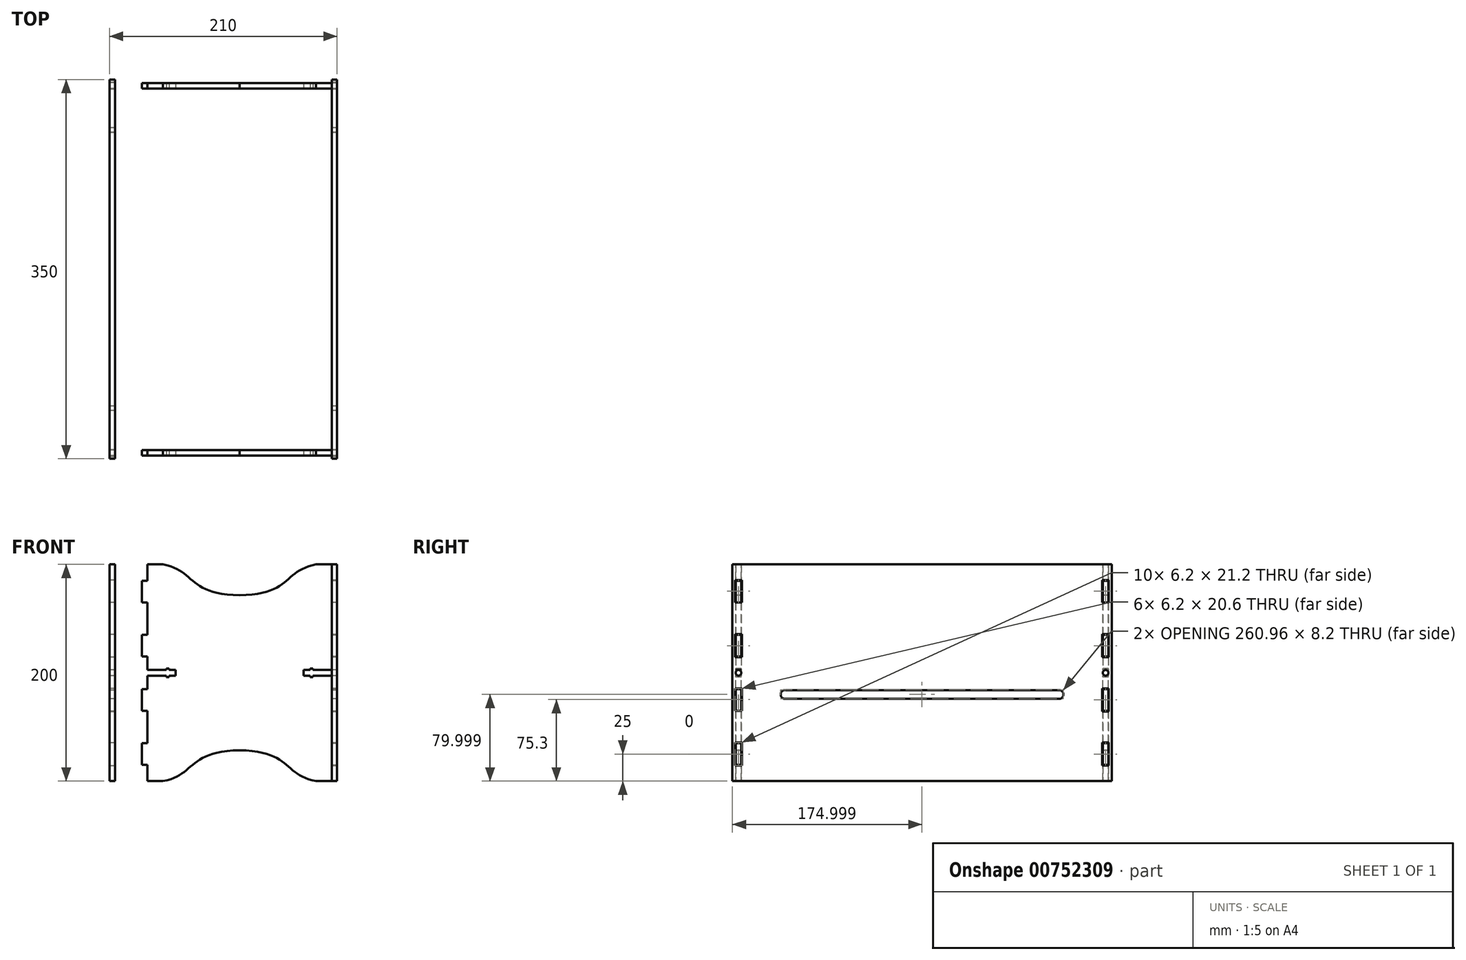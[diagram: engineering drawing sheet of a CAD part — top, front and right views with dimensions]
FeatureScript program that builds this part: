
annotation { "Feature Type Name" : "Feature", "Feature Type Description" : "" }
export const myFeature = defineFeature(function(context is Context, id is Id, definition is map)
    precondition{}
    {
        {
            var Q0;
            Q0=qCreatedBy(makeId("Right.planeOp"),FACE);
            var sketch = newSketch(context, id + "F0", { "sketchPlane" : qUnion([Q0])});
            skLineSegment(sketch, "E0.bottom", {"start": v(175, -100) * mm, "end": v(-175, -100) * mm});
            skLineSegment(sketch, "E0.top", {"start": v(175, 100) * mm, "end": v(4, 100) * mm});
            skLineSegment(sketch, "E0.left", {"start": v(175, -100) * mm, "end": v(175, 100) * mm});
            skLineSegment(sketch, "E0.right", {"start": v(-175, -100) * mm, "end": v(-175, 100) * mm});
            skPoint(sketch, "E0.middle", {"position": v(0, 0) * mm});
            skLineSegment(sketch, "E1", {"start": v(0, 80) * mm, "end": v(0, -100) * mm, "construction": true});
            skLineSegment(sketch, "E2", {"start": v(-175, 0) * mm, "end": v(175, 0) * mm, "construction": true});
            skLineSegment(sketch, "E3.trimOffspring", {"start": v(-4, 100) * mm, "end": v(-175, 100) * mm});
            skLineSegment(sketch, "E4", {"start": v(-172, 100) * mm, "end": v(-172, 85) * mm, "construction": true});
            skLineSegment(sketch, "E5", {"start": v(-166.8, 65) * mm, "end": v(-166.8, 35) * mm, "construction": true});
            skLineSegment(sketch, "E6.bottom", {"start": v(-172, 85) * mm, "end": v(-166.8, 85) * mm});
            skLineSegment(sketch, "E6.top", {"start": v(-172, 65) * mm, "end": v(-166.8, 65) * mm});
            skLineSegment(sketch, "E6.left", {"start": v(-172, 85) * mm, "end": v(-172, 65) * mm});
            skLineSegment(sketch, "E6.right", {"start": v(-166.8, 85) * mm, "end": v(-166.8, 65) * mm});
            skLineSegment(sketch, "E7.bottom", {"start": v(-172, 35) * mm, "end": v(-166.8, 35) * mm});
            skLineSegment(sketch, "E7.top", {"start": v(-172, 15) * mm, "end": v(-166.8, 15) * mm});
            skLineSegment(sketch, "E7.left", {"start": v(-172, 35) * mm, "end": v(-172, 15) * mm});
            skLineSegment(sketch, "E7.right", {"start": v(-166.8, 35) * mm, "end": v(-166.8, 15) * mm});
            skLineSegment(sketch, "E8", {"start": v(-169.4, 65) * mm, "end": v(-169.4, 35) * mm, "construction": true});
            skPoint(sketch, "E9", {"position": v(-169.4, 50) * mm});
            skLineSegment(sketch, "E10.MirrorCS", {"start": v(-172, -85) * mm, "end": v(-166.8, -85) * mm});
            skPoint(sketch, "E11.orphan", {"position": v(-166.8, 100) * mm});
            skLineSegment(sketch, "E12.trimOffspring", {"start": v(-172, 65) * mm, "end": v(-172, 35) * mm, "construction": true});
            skLineSegment(sketch, "E13.MirrorCS", {"start": v(-166.8, -85) * mm, "end": v(-166.8, -65) * mm});
            skLineSegment(sketch, "E14.MirrorCS", {"start": v(-172, -85) * mm, "end": v(-172, -65) * mm});
            skLineSegment(sketch, "E15.MirrorCS", {"start": v(-172, -65) * mm, "end": v(-166.8, -65) * mm});
            skLineSegment(sketch, "E16.MirrorCS", {"start": v(-172, -35) * mm, "end": v(-166.8, -35) * mm});
            skLineSegment(sketch, "E17.MirrorCS", {"start": v(-172, -15) * mm, "end": v(-166.8, -15) * mm});
            skLineSegment(sketch, "E18.trimOffspring", {"start": v(-172, 0) * mm, "end": v(-172, -15) * mm, "construction": true});
            skLineSegment(sketch, "E19.trimOffspring", {"start": v(-166.8, 0) * mm, "end": v(-166.8, -15) * mm, "construction": true});
            skLineSegment(sketch, "E20.MirrorCS", {"start": v(-172, -35) * mm, "end": v(-172, -15) * mm});
            skLineSegment(sketch, "E21.MirrorCS", {"start": v(-166.8, -35) * mm, "end": v(-166.8, -15) * mm});
            skLineSegment(sketch, "E22.trimOffspring", {"start": v(-172, -35) * mm, "end": v(-172, -65) * mm, "construction": true});
            skLineSegment(sketch, "E23.trimOffspring", {"start": v(-166.8, -35) * mm, "end": v(-166.8, -65) * mm, "construction": true});
            skLineSegment(sketch, "E24.trimOffspring", {"start": v(-166.8, -85) * mm, "end": v(-166.8, -100) * mm, "construction": true});
            skLineSegment(sketch, "E25.trimOffspring", {"start": v(-172, -85) * mm, "end": v(-172, -100) * mm, "construction": true});
            skLineSegment(sketch, "E26.MirrorCS", {"start": v(172, 85) * mm, "end": v(172, 65) * mm});
            skLineSegment(sketch, "E27.MirrorCS", {"start": v(166.8, 85) * mm, "end": v(166.8, 65) * mm});
            skLineSegment(sketch, "E28.MirrorCS", {"start": v(172, 85) * mm, "end": v(166.8, 85) * mm});
            skLineSegment(sketch, "E29.MirrorCS", {"start": v(172, 65) * mm, "end": v(166.8, 65) * mm});
            skLineSegment(sketch, "E30.MirrorCS", {"start": v(172, 35) * mm, "end": v(166.8, 35) * mm});
            skLineSegment(sketch, "E31.MirrorCS", {"start": v(166.8, 35) * mm, "end": v(166.8, 15) * mm});
            skLineSegment(sketch, "E32.MirrorCS", {"start": v(172, 35) * mm, "end": v(172, 15) * mm});
            skLineSegment(sketch, "E33.MirrorCS", {"start": v(172, 15) * mm, "end": v(166.8, 15) * mm});
            skLineSegment(sketch, "E34.MirrorCS", {"start": v(172, -15) * mm, "end": v(166.8, -15) * mm});
            skLineSegment(sketch, "E35.MirrorCS", {"start": v(166.8, -35) * mm, "end": v(166.8, -15) * mm});
            skLineSegment(sketch, "E36.MirrorCS", {"start": v(172, -35) * mm, "end": v(172, -15) * mm});
            skLineSegment(sketch, "E37.MirrorCS", {"start": v(172, -35) * mm, "end": v(166.8, -35) * mm});
            skLineSegment(sketch, "E38.MirrorCS", {"start": v(172, -65) * mm, "end": v(166.8, -65) * mm});
            skLineSegment(sketch, "E39.MirrorCS", {"start": v(172, -85) * mm, "end": v(166.8, -85) * mm});
            skLineSegment(sketch, "E40.MirrorCS", {"start": v(166.8, -85) * mm, "end": v(166.8, -65) * mm});
            skLineSegment(sketch, "E41.MirrorCS", {"start": v(172, -85) * mm, "end": v(172, -65) * mm});
            skCircle(sketch, "E42", {"center": v(-126.38, -20) * mm, "radius": 4.1 * mm});
            skLineSegment(sketch, "E43.left", {"start": v(-126.26, -15.9) * mm, "end": v(-126.26, -24.1) * mm});
            skPoint(sketch, "E44.left.end.orphan", {"position": v(4, 80) * mm});
            skPoint(sketch, "E44.right.end.orphan", {"position": v(-4, 80) * mm});
            skLineSegment(sketch, "E45", {"start": v(-4, 100) * mm, "end": v(4, 100) * mm});
            skCircle(sketch, "E46", {"center": v(0, 80) * mm, "radius": 150 * mm, "construction": true});
            skPoint(sketch, "E43.right.end.orphan", {"position": v(140.09, -4.1) * mm});
            skPoint(sketch, "E47.center.orphan", {"position": v(140.09, 0) * mm});
            skCircle(sketch, "E48", {"center": v(-126.38, -20) * mm, "radius": 11 * mm, "construction": true});
            skCircle(sketch, "E49", {"center": v(126.38, -20) * mm, "radius": 4.1 * mm});
            skLineSegment(sketch, "E50.left", {"start": v(126.5, -15.9) * mm, "end": v(126.5, -24.1) * mm});
            skCircle(sketch, "E51", {"center": v(126.38, -20) * mm, "radius": 11 * mm, "construction": true});
            skLineSegment(sketch, "E52.bottom", {"start": v(126.5, -15.9) * mm, "end": v(-126.26, -15.9) * mm});
            skLineSegment(sketch, "E52.top", {"start": v(126.5, -24.1) * mm, "end": v(-126.26, -24.1) * mm});
            skCircle(sketch, "E53", {"center": v(-169.4, 0) * mm, "radius": 2.6 * mm});
            skCircle(sketch, "E54.MirrorC", {"center": v(169.4, 0) * mm, "radius": 2.6 * mm});
            skSolve(sketch);
        }
        {
            var Q0;
            Q0=qSketchRegion(id+"F0",true);
            extrude(context, id + "F1", {"entities" : qUnion([Q0]), "depth" : 5 * mm});
        }
        {
            var Q0;
            Q0=makeQuery(id+"F1.opExtrude","SWEPT_FACE",FACE,{"disambiguationData":[OSD([sQuery(id+"F0.wireOp",EDGE,"E27.MirrorCS")])]});
            var sketch = newSketch(context, id + "F2", { "sketchPlane" : qUnion([Q0])});
            skPoint(sketch, "E55.0", {"position": v(-5, 100) * mm});
            skLineSegment(sketch, "E56.bottom", {"start": v(0, 100) * mm, "end": v(14.33, 100) * mm});
            skLineSegment(sketch, "E56.top", {"start": v(0, -100) * mm, "end": v(14.33, -100) * mm});
            skLineSegment(sketch, "E56.left", {"start": v(-5, 85) * mm, "end": v(-5, 65) * mm});
            skLineSegment(sketch, "E56.right", {"start": v(170, 100) * mm, "end": v(170, 52.6) * mm});
            skPoint(sketch, "E57.middle", {"position": v(18.7, -50) * mm});
            skPoint(sketch, "E57.centerSnap0", {"position": v(26, -50) * mm});
            skLineSegment(sketch, "E58.0", {"start": v(0, 85) * mm, "end": v(0, 65) * mm, "construction": true});
            skLineSegment(sketch, "E58.1", {"start": v(0, 35) * mm, "end": v(0, 15) * mm, "construction": true});
            skLineSegment(sketch, "E58.2", {"start": v(0, -35) * mm, "end": v(0, -15) * mm, "construction": true});
            skLineSegment(sketch, "E58.3", {"start": v(0, -85) * mm, "end": v(0, -65) * mm, "construction": true});
            skLineSegment(sketch, "E59.bottom", {"start": v(0, 85) * mm, "end": v(-5, 85) * mm});
            skLineSegment(sketch, "E59.left", {"start": v(0, 85) * mm, "end": v(0, 100) * mm});
            skLineSegment(sketch, "E60.bottom", {"start": v(0, 65) * mm, "end": v(-5, 65) * mm});
            skLineSegment(sketch, "E60.top", {"start": v(0, 35) * mm, "end": v(-5, 35) * mm});
            skLineSegment(sketch, "E60.left", {"start": v(0, 65) * mm, "end": v(0, 52.6) * mm});
            skLineSegment(sketch, "E61.bottom", {"start": v(0, 15) * mm, "end": v(0, 15) * mm});
            skLineSegment(sketch, "E61.top", {"start": v(0, -15) * mm, "end": v(0, -15) * mm});
            skLineSegment(sketch, "E61.right", {"start": v(0, 15) * mm, "end": v(0, 2.6) * mm});
            skLineSegment(sketch, "E62.bottom", {"start": v(-5, -15) * mm, "end": v(0, -15) * mm});
            skLineSegment(sketch, "E62.top", {"start": v(-5, 15) * mm, "end": v(0, 15) * mm});
            skLineSegment(sketch, "E62.right", {"start": v(0, -15) * mm, "end": v(0, -2.6) * mm});
            skLineSegment(sketch, "E63", {"start": v(0, -35) * mm, "end": v(-5, -35) * mm});
            skLineSegment(sketch, "E64", {"start": v(0, -85) * mm, "end": v(-5, -85) * mm});
            skLineSegment(sketch, "E65", {"start": v(0, -65) * mm, "end": v(-5, -65) * mm});
            skLineSegment(sketch, "E66.trimOffspring", {"start": v(-5, -15) * mm, "end": v(-5, -35) * mm});
            skLineSegment(sketch, "E67.trimOffspring", {"start": v(-5, -65) * mm, "end": v(-5, -85) * mm});
            skLineSegment(sketch, "E68", {"start": v(0, -85) * mm, "end": v(0, -100) * mm});
            skLineSegment(sketch, "E69", {"start": v(0, -52.6) * mm, "end": v(0, -65) * mm});
            skLineSegment(sketch, "E70", {"start": v(0, -47.4) * mm, "end": v(0, -35) * mm});
            skLineSegment(sketch, "E71", {"start": v(0, 35) * mm, "end": v(0, 47.4) * mm});
            skLineSegment(sketch, "E72", {"start": v(0, 52.6) * mm, "end": v(0, 65) * mm});
            skLineSegment(sketch, "E73.trimOffspring", {"start": v(0, 47.4) * mm, "end": v(0, 35) * mm});
            skLineSegment(sketch, "E74", {"start": v(-5, 65) * mm, "end": v(0, 65) * mm});
            skLineSegment(sketch, "E75.trimOffspring", {"start": v(-5, 35) * mm, "end": v(-5, 15) * mm});
            skLineSegment(sketch, "E76", {"start": v(85, 100) * mm, "end": v(85, -100) * mm, "construction": true});
            skLineSegment(sketch, "E77.MirrorCS", {"start": v(175, 65) * mm, "end": v(170, 65) * mm});
            skLineSegment(sketch, "E78.MirrorCS", {"start": v(170, 65) * mm, "end": v(175, 65) * mm});
            skLineSegment(sketch, "E79.MirrorCS", {"start": v(170, 85) * mm, "end": v(175, 85) * mm});
            skLineSegment(sketch, "E80.MirrorCS", {"start": v(175, -15) * mm, "end": v(170, -15) * mm});
            skLineSegment(sketch, "E81.MirrorCS", {"start": v(170, -15) * mm, "end": v(170, -2.6) * mm});
            skLineSegment(sketch, "E82.MirrorCS", {"start": v(175, 15) * mm, "end": v(170, 15) * mm});
            skLineSegment(sketch, "E83.MirrorCS", {"start": v(170, -35) * mm, "end": v(175, -35) * mm});
            skLineSegment(sketch, "E84.MirrorCS", {"start": v(170, 35) * mm, "end": v(175, 35) * mm});
            skLineSegment(sketch, "E85.MirrorCS", {"start": v(170, -65) * mm, "end": v(175, -65) * mm});
            skLineSegment(sketch, "E86.MirrorCS", {"start": v(170, -85) * mm, "end": v(175, -85) * mm});
            skLineSegment(sketch, "E87.MirrorCS", {"start": v(170, 52.6) * mm, "end": v(170, 65) * mm});
            skLineSegment(sketch, "E88.MirrorCS", {"start": v(170, 35) * mm, "end": v(170, 47.4) * mm});
            skLineSegment(sketch, "E89.MirrorCS", {"start": v(175, 85) * mm, "end": v(175, 65) * mm});
            skLineSegment(sketch, "E90.MirrorCS", {"start": v(170, 100) * mm, "end": v(170, 15) * mm});
            skLineSegment(sketch, "E91.MirrorCS", {"start": v(170, -15) * mm, "end": v(170, -15) * mm});
            skLineSegment(sketch, "E92.MirrorCS", {"start": v(170, 85) * mm, "end": v(170, 100) * mm});
            skPoint(sketch, "E93.MirrorP", {"position": v(175, 100) * mm});
            skLineSegment(sketch, "E94.MirrorCS", {"start": v(170, -47.4) * mm, "end": v(170, -35) * mm});
            skLineSegment(sketch, "E95.MirrorCS", {"start": v(175, -15) * mm, "end": v(175, -35) * mm});
            skLineSegment(sketch, "E96.MirrorCS", {"start": v(170, 47.4) * mm, "end": v(170, 35) * mm});
            skLineSegment(sketch, "E97.MirrorCS", {"start": v(170, -85) * mm, "end": v(170, -100) * mm});
            skLineSegment(sketch, "E98.MirrorCS", {"start": v(170, 15) * mm, "end": v(170, 15) * mm});
            skLineSegment(sketch, "E99.MirrorCS", {"start": v(170, -52.6) * mm, "end": v(170, -65) * mm});
            skLineSegment(sketch, "E100.MirrorCS", {"start": v(170, 65) * mm, "end": v(170, 52.6) * mm});
            skLineSegment(sketch, "E101.MirrorCS", {"start": v(175, 35) * mm, "end": v(175, 15) * mm});
            skLineSegment(sketch, "E102.MirrorCS", {"start": v(175, -65) * mm, "end": v(175, -85) * mm});
            skLineSegment(sketch, "E103.MirrorCS", {"start": v(170, 85) * mm, "end": v(170, 65) * mm, "construction": true});
            skFitSpline(sketch, "E104", {"points": [v(14.33, 100) * mm, v(85, 71.5) * mm], "startDerivative": vector(91.37, -16.34) * mm, "endDerivative": vector(146.95, -3.2) * mm});
            skFitSpline(sketch, "E105.MirrorCS", {"points": [v(155.67, 100) * mm, v(85, 71.5) * mm], "startDerivative": vector(-91.37, -16.34) * mm, "endDerivative": vector(-146.95, -3.2) * mm});
            skLineSegment(sketch, "E106.trimOffspring", {"start": v(155.67, 100) * mm, "end": v(170, 100) * mm});
            skLineSegment(sketch, "E107", {"start": v(85, 0) * mm, "end": v(170, 0) * mm, "construction": true});
            skFitSpline(sketch, "E108.MirrorCS", {"points": [v(155.67, -100) * mm, v(85, -71.5) * mm], "startDerivative": vector(-91.37, 16.34) * mm, "endDerivative": vector(-146.95, 3.2) * mm});
            skFitSpline(sketch, "E109.MirrorCS", {"points": [v(14.33, -100) * mm, v(85, -71.5) * mm], "startDerivative": vector(91.37, 16.34) * mm, "endDerivative": vector(146.95, 3.2) * mm});
            skLineSegment(sketch, "E110.trimOffspring", {"start": v(155.67, -100) * mm, "end": v(170, -100) * mm});
            skLineSegment(sketch, "E111.trimOffspring", {"start": v(170, 42.3) * mm, "end": v(170, 2.6) * mm});
            skLineSegment(sketch, "E112.bottom", {"start": v(0, 2.6) * mm, "end": v(17.4, 2.6) * mm});
            skLineSegment(sketch, "E112.top", {"start": v(0, -2.6) * mm, "end": v(17.4, -2.6) * mm});
            skLineSegment(sketch, "E112.right", {"start": v(26, 2.6) * mm, "end": v(26, -2.6) * mm});
            skLineSegment(sketch, "E113.bottom", {"start": v(20, -4.05) * mm, "end": v(17.4, -4.05) * mm});
            skLineSegment(sketch, "E113.top", {"start": v(20, 4.05) * mm, "end": v(17.4, 4.05) * mm});
            skLineSegment(sketch, "E113.left", {"start": v(20, -4.05) * mm, "end": v(20, -2.6) * mm});
            skLineSegment(sketch, "E113.right", {"start": v(17.4, -4.05) * mm, "end": v(17.4, -2.6) * mm});
            skPoint(sketch, "E113.middle", {"position": v(18.7, 0) * mm});
            skPoint(sketch, "E113.middle.positionSnap0", {"position": v(26, 0) * mm});
            skPoint(sketch, "E113.centerSnap0", {"position": v(26, 0) * mm});
            skLineSegment(sketch, "E114.trimOffspring", {"start": v(17.4, 2.6) * mm, "end": v(17.4, 4.05) * mm});
            skLineSegment(sketch, "E115.trimOffspring", {"start": v(20, 2.6) * mm, "end": v(26, 2.6) * mm});
            skLineSegment(sketch, "E116.trimOffspring", {"start": v(20, 2.6) * mm, "end": v(20, 4.05) * mm});
            skLineSegment(sketch, "E117.trimOffspring", {"start": v(20, -2.6) * mm, "end": v(26, -2.6) * mm});
            skPoint(sketch, "E118.MirrorP", {"position": v(174, 0) * mm});
            skLineSegment(sketch, "E119.MirrorCS", {"start": v(170, 92.3) * mm, "end": v(170, 79.9) * mm});
            skPoint(sketch, "E120.MirrorP", {"position": v(181.3, 0) * mm});
            skLineSegment(sketch, "E121", {"start": v(0, 52.6) * mm, "end": v(0, 47.4) * mm});
            skLineSegment(sketch, "E122", {"start": v(0, -47.4) * mm, "end": v(0, -52.6) * mm});
            skLineSegment(sketch, "E123", {"start": v(170, -52.6) * mm, "end": v(170, -47.4) * mm});
            skLineSegment(sketch, "E124", {"start": v(170, 47.4) * mm, "end": v(170, 52.6) * mm});
            skLineSegment(sketch, "E125.trimOffspring", {"start": v(0, -2.6) * mm, "end": v(0, -15) * mm});
            skLineSegment(sketch, "E126.trimOffspring", {"start": v(170, 92.3) * mm, "end": v(170, 2.6) * mm});
            skLineSegment(sketch, "E127.trimOffspring", {"start": v(170, 15) * mm, "end": v(170, 100) * mm});
            skLineSegment(sketch, "E128.trimOffspring", {"start": v(0, 2.6) * mm, "end": v(0, 15) * mm});
            skLineSegment(sketch, "E129.bottom", {"start": v(170, -2.6) * mm, "end": v(152.6, -2.6) * mm});
            skLineSegment(sketch, "E129.top", {"start": v(170, 2.6) * mm, "end": v(152.6, 2.6) * mm});
            skLineSegment(sketch, "E129.right", {"start": v(144, -2.6) * mm, "end": v(144, 2.6) * mm});
            skLineSegment(sketch, "E130.bottom", {"start": v(150, 4.05) * mm, "end": v(152.6, 4.05) * mm});
            skLineSegment(sketch, "E130.top", {"start": v(150, -4.05) * mm, "end": v(152.6, -4.05) * mm});
            skLineSegment(sketch, "E130.left", {"start": v(150, 4.05) * mm, "end": v(150, 2.6) * mm});
            skLineSegment(sketch, "E130.right", {"start": v(152.6, 4.05) * mm, "end": v(152.6, 2.6) * mm});
            skLineSegment(sketch, "E131.trimOffspring", {"start": v(152.6, -2.6) * mm, "end": v(152.6, -4.05) * mm});
            skLineSegment(sketch, "E132.trimOffspring", {"start": v(150, -2.6) * mm, "end": v(144, -2.6) * mm});
            skLineSegment(sketch, "E133.trimOffspring", {"start": v(150, -2.6) * mm, "end": v(150, -4.05) * mm});
            skLineSegment(sketch, "E134.trimOffspring", {"start": v(150, 2.6) * mm, "end": v(144, 2.6) * mm});
            skLineSegment(sketch, "E135.trimOffspring", {"start": v(170, -2.6) * mm, "end": v(170, -47.4) * mm});
            skLineSegment(sketch, "E136.trimOffspring", {"start": v(170, -2.6) * mm, "end": v(170, -15) * mm});
            skLineSegment(sketch, "E137.trimOffspring", {"start": v(170, 2.6) * mm, "end": v(170, 92.3) * mm});
            skLineSegment(sketch, "E138.trimOffspring", {"start": v(170, -2.6) * mm, "end": v(170, -100) * mm});
            skSolve(sketch);
        }
        {
            var Q0;
            Q0=qSketchRegion(id+"F2",true);
            extrude(context, id + "F3", {"entities" : qUnion([Q0]), "depth" : 5 * mm});
        }
        {
            var Q0;
            Q0=makeQuery(id+"F3.opExtrude","SWEPT_BODY",BODY,{"disambiguationData":[OSD([sQuery(id+"F2.wireOp",EDGE,"E56.bottom"),sQuery(id+"F2.wireOp",EDGE,"E56.top"),sQuery(id+"F2.wireOp",EDGE,"SfhTXy7u-tcII-MEaY-9RSd-v6Q0Sdl2hSPR.bottom"),sQuery(id+"F2.wireOp",EDGE,"SfhTXy7u-tcII-MEaY-9RSd-v6Q0Sdl2hSPR.top"),sQuery(id+"F2.wireOp",EDGE,"SfhTXy7u-tcII-MEaY-9RSd-v6Q0Sdl2hSPR.right"),sQuery(id+"F2.wireOp",EDGE,"RLKNdBM9-fcir-abDg-scLo-AlFl0wZaGOfU.bottom"),sQuery(id+"F2.wireOp",EDGE,"RLKNdBM9-fcir-abDg-scLo-AlFl0wZaGOfU.top"),sQuery(id+"F2.wireOp",EDGE,"RLKNdBM9-fcir-abDg-scLo-AlFl0wZaGOfU.left"),sQuery(id+"F2.wireOp",EDGE,"RLKNdBM9-fcir-abDg-scLo-AlFl0wZaGOfU.right"),sQuery(id+"F2.wireOp",EDGE,"592e8475-5e9e-4e55-86be-326854908ba4.bottom"),sQuery(id+"F2.wireOp",EDGE,"592e8475-5e9e-4e55-86be-326854908ba4.top"),sQuery(id+"F2.wireOp",EDGE,"592e8475-5e9e-4e55-86be-326854908ba4.right"),sQuery(id+"F2.wireOp",EDGE,"E57.bottom"),sQuery(id+"F2.wireOp",EDGE,"E57.top"),sQuery(id+"F2.wireOp",EDGE,"E57.left"),sQuery(id+"F2.wireOp",EDGE,"E57.right"),sQuery(id+"F2.wireOp",EDGE,"98f910ef-10bf-4355-9089-b64edb675ca1.trimOffspring"),sQuery(id+"F2.wireOp",EDGE,"7f1d8590-854d-48a8-a345-113ac86432ce.trimOffspring"),sQuery(id+"F2.wireOp",EDGE,"8eb6f7d6-6f97-4ebc-a51c-8934afb20485.trimOffspring"),sQuery(id+"F2.wireOp",EDGE,"79887d4c-0bb1-4e3d-a504-848fb675985f.trimOffspring"),sQuery(id+"F2.wireOp",EDGE,"6021e146-63f0-49d4-b214-f61fa3b2a401.trimOffspring"),sQuery(id+"F2.wireOp",EDGE,"bdb7ae41-a7ed-46e7-8485-b54428fed669.trimOffspring"),sQuery(id+"F2.wireOp",EDGE,"45a4283d-6044-4d88-b901-0b074d01a6ab.trimOffspring"),sQuery(id+"F2.wireOp",EDGE,"59fc1645-d4a0-4682-934b-e6e005b09d3d.trimOffspring"),sQuery(id+"F2.wireOp",EDGE,"E59.bottom"),sQuery(id+"F2.wireOp",EDGE,"E59.left"),sQuery(id+"F2.wireOp",EDGE,"E60.top"),sQuery(id+"F2.wireOp",EDGE,"E62.bottom"),sQuery(id+"F2.wireOp",EDGE,"E62.top"),sQuery(id+"F2.wireOp",EDGE,"E62.right"),sQuery(id+"F2.wireOp",EDGE,"E63"),sQuery(id+"F2.wireOp",EDGE,"E64"),sQuery(id+"F2.wireOp",EDGE,"E65"),sQuery(id+"F2.wireOp",EDGE,"E66.trimOffspring"),sQuery(id+"F2.wireOp",EDGE,"E67.trimOffspring"),sQuery(id+"F2.wireOp",EDGE,"E68"),sQuery(id+"F2.wireOp",EDGE,"E69"),sQuery(id+"F2.wireOp",EDGE,"E70"),sQuery(id+"F2.wireOp",EDGE,"E72"),sQuery(id+"F2.wireOp",EDGE,"E73.trimOffspring"),sQuery(id+"F2.wireOp",EDGE,"E56.left"),sQuery(id+"F2.wireOp",EDGE,"E74"),sQuery(id+"F2.wireOp",EDGE,"E75.trimOffspring"),sQuery(id+"F2.wireOp",EDGE,"729de1fe-793c-4f06-af17-d50d40598c080.MirrorCS"),sQuery(id+"F2.wireOp",EDGE,"729de1fe-793c-4f06-af17-d50d40598c082.MirrorCS"),sQuery(id+"F2.wireOp",EDGE,"729de1fe-793c-4f06-af17-d50d40598c083.MirrorCS"),sQuery(id+"F2.wireOp",EDGE,"729de1fe-793c-4f06-af17-d50d40598c084.MirrorCS"),sQuery(id+"F2.wireOp",EDGE,"729de1fe-793c-4f06-af17-d50d40598c085.MirrorCS"),sQuery(id+"F2.wireOp",EDGE,"729de1fe-793c-4f06-af17-d50d40598c086.MirrorCS"),sQuery(id+"F2.wireOp",EDGE,"729de1fe-793c-4f06-af17-d50d40598c087.MirrorCS"),sQuery(id+"F2.wireOp",EDGE,"729de1fe-793c-4f06-af17-d50d40598c088.MirrorCS"),sQuery(id+"F2.wireOp",EDGE,"729de1fe-793c-4f06-af17-d50d40598c089.MirrorCS"),sQuery(id+"F2.wireOp",EDGE,"E770.MirrorCS"),sQuery(id+"F2.wireOp",EDGE,"E78.MirrorCS"),sQuery(id+"F2.wireOp",EDGE,"E772.MirrorCS"),sQuery(id+"F2.wireOp",EDGE,"E79.MirrorCS"),sQuery(id+"F2.wireOp",EDGE,"E774.MirrorCS"),sQuery(id+"F2.wireOp",EDGE,"E775.MirrorCS"),sQuery(id+"F2.wireOp",EDGE,"E776.MirrorCS"),sQuery(id+"F2.wireOp",EDGE,"E777.MirrorCS"),sQuery(id+"F2.wireOp",EDGE,"E778.MirrorCS"),sQuery(id+"F2.wireOp",EDGE,"E779.MirrorCS"),sQuery(id+"F2.wireOp",EDGE,"729de1fe-793c-4f06-af17-d50d40598c0820.MirrorCS"),sQuery(id+"F2.wireOp",EDGE,"E80.MirrorCS"),sQuery(id+"F2.wireOp",EDGE,"E82.MirrorCS"),sQuery(id+"F2.wireOp",EDGE,"E83.MirrorCS"),sQuery(id+"F2.wireOp",EDGE,"E84.MirrorCS"),sQuery(id+"F2.wireOp",EDGE,"E85.MirrorCS"),sQuery(id+"F2.wireOp",EDGE,"E86.MirrorCS"),sQuery(id+"F2.wireOp",EDGE,"E92.MirrorCS"),sQuery(id+"F2.wireOp",EDGE,"729de1fe-793c-4f06-af17-d50d40598c0837.MirrorCS"),sQuery(id+"F2.wireOp",EDGE,"729de1fe-793c-4f06-af17-d50d40598c0838.MirrorCS"),sQuery(id+"F2.wireOp",EDGE,"729de1fe-793c-4f06-af17-d50d40598c0841.MirrorCS"),sQuery(id+"F2.wireOp",EDGE,"E95.MirrorCS"),sQuery(id+"F2.wireOp",EDGE,"729de1fe-793c-4f06-af17-d50d40598c0851.MirrorCS"),sQuery(id+"F2.wireOp",EDGE,"E89.MirrorCS"),sQuery(id+"F2.wireOp",EDGE,"E100.MirrorCS"),sQuery(id+"F2.wireOp",EDGE,"E101.MirrorCS"),sQuery(id+"F2.wireOp",EDGE,"E102.MirrorCS"),sQuery(id+"F2.wireOp",EDGE,"E104"),sQuery(id+"F2.wireOp",EDGE,"E105.MirrorCS"),sQuery(id+"F2.wireOp",EDGE,"E106.trimOffspring"),sQuery(id+"F2.wireOp",EDGE,"E108.MirrorCS"),sQuery(id+"F2.wireOp",EDGE,"E109.MirrorCS"),sQuery(id+"F2.wireOp",EDGE,"E110.trimOffspring"),sQuery(id+"F2.wireOp",EDGE,"31b2c9c2-f7eb-4751-8350-943a16306e17.trimOffspring"),sQuery(id+"F2.wireOp",EDGE,"E111.trimOffspring")])]});
            var Q1;
            Q1=makeQuery(id+"F1.opExtrude","SWEPT_BODY",BODY,{"disambiguationData":[OSD([sQuery(id+"F0.wireOp",EDGE,"E0.bottom"),sQuery(id+"F0.wireOp",EDGE,"E0.top"),sQuery(id+"F0.wireOp",EDGE,"E0.left"),sQuery(id+"F0.wireOp",EDGE,"E0.right"),sQuery(id+"F0.wireOp",EDGE,"E3.trimOffspring"),sQuery(id+"F0.wireOp",EDGE,"E6.bottom"),sQuery(id+"F0.wireOp",EDGE,"E6.top"),sQuery(id+"F0.wireOp",EDGE,"E6.left"),sQuery(id+"F0.wireOp",EDGE,"E6.right"),sQuery(id+"F0.wireOp",EDGE,"E7.bottom"),sQuery(id+"F0.wireOp",EDGE,"E7.top"),sQuery(id+"F0.wireOp",EDGE,"E7.left"),sQuery(id+"F0.wireOp",EDGE,"E7.right"),sQuery(id+"F0.wireOp",EDGE,"1BBTkZs5-luX3-xtZO-tfno-nD7ZldyCOrRv"),sQuery(id+"F0.wireOp",EDGE,"E13.MirrorCS"),sQuery(id+"F0.wireOp",EDGE,"E14.MirrorCS"),sQuery(id+"F0.wireOp",EDGE,"E10.MirrorCS"),sQuery(id+"F0.wireOp",EDGE,"E15.MirrorCS"),sQuery(id+"F0.wireOp",EDGE,"edba22f7-fcec-4b76-9e19-08ec19d2e6a00.MirrorC"),sQuery(id+"F0.wireOp",EDGE,"E16.MirrorCS"),sQuery(id+"F0.wireOp",EDGE,"E17.MirrorCS"),sQuery(id+"F0.wireOp",EDGE,"E20.MirrorCS"),sQuery(id+"F0.wireOp",EDGE,"E21.MirrorCS"),sQuery(id+"F0.wireOp",EDGE,"E26.MirrorCS"),sQuery(id+"F0.wireOp",EDGE,"E27.MirrorCS"),sQuery(id+"F0.wireOp",EDGE,"E28.MirrorCS"),sQuery(id+"F0.wireOp",EDGE,"E29.MirrorCS"),sQuery(id+"F0.wireOp",EDGE,"e9cac41d-f357-42ad-afaa-485d0ff043840.MirrorC"),sQuery(id+"F0.wireOp",EDGE,"E30.MirrorCS"),sQuery(id+"F0.wireOp",EDGE,"E31.MirrorCS"),sQuery(id+"F0.wireOp",EDGE,"E32.MirrorCS"),sQuery(id+"F0.wireOp",EDGE,"E33.MirrorCS"),sQuery(id+"F0.wireOp",EDGE,"E34.MirrorCS"),sQuery(id+"F0.wireOp",EDGE,"E35.MirrorCS"),sQuery(id+"F0.wireOp",EDGE,"E36.MirrorCS"),sQuery(id+"F0.wireOp",EDGE,"E37.MirrorCS"),sQuery(id+"F0.wireOp",EDGE,"f40b6c40-3a45-4a40-b477-66a71d50dfa00.MirrorC"),sQuery(id+"F0.wireOp",EDGE,"E38.MirrorCS"),sQuery(id+"F0.wireOp",EDGE,"E39.MirrorCS"),sQuery(id+"F0.wireOp",EDGE,"E40.MirrorCS"),sQuery(id+"F0.wireOp",EDGE,"E41.MirrorCS"),sQuery(id+"F0.wireOp",EDGE,"E44.left"),sQuery(id+"F0.wireOp",EDGE,"E44.right"),sQuery(id+"F0.wireOp",EDGE,"eyhBYY9M-95YG-LpN2-QZ7T-SWmW0xq0itgo")])]});
            var Q2;
            Q2=makeQuery(id+"F3.opExtrude","CAP_FACE",FACE,{"disambiguationData":[OSD([sQuery(id+"F2.wireOp",EDGE,"E56.bottom"),sQuery(id+"F2.wireOp",EDGE,"E56.top"),sQuery(id+"F2.wireOp",EDGE,"SfhTXy7u-tcII-MEaY-9RSd-v6Q0Sdl2hSPR.bottom"),sQuery(id+"F2.wireOp",EDGE,"SfhTXy7u-tcII-MEaY-9RSd-v6Q0Sdl2hSPR.top"),sQuery(id+"F2.wireOp",EDGE,"SfhTXy7u-tcII-MEaY-9RSd-v6Q0Sdl2hSPR.right"),sQuery(id+"F2.wireOp",EDGE,"RLKNdBM9-fcir-abDg-scLo-AlFl0wZaGOfU.bottom"),sQuery(id+"F2.wireOp",EDGE,"RLKNdBM9-fcir-abDg-scLo-AlFl0wZaGOfU.top"),sQuery(id+"F2.wireOp",EDGE,"RLKNdBM9-fcir-abDg-scLo-AlFl0wZaGOfU.left"),sQuery(id+"F2.wireOp",EDGE,"RLKNdBM9-fcir-abDg-scLo-AlFl0wZaGOfU.right"),sQuery(id+"F2.wireOp",EDGE,"592e8475-5e9e-4e55-86be-326854908ba4.bottom"),sQuery(id+"F2.wireOp",EDGE,"592e8475-5e9e-4e55-86be-326854908ba4.top"),sQuery(id+"F2.wireOp",EDGE,"592e8475-5e9e-4e55-86be-326854908ba4.right"),sQuery(id+"F2.wireOp",EDGE,"E57.bottom"),sQuery(id+"F2.wireOp",EDGE,"E57.top"),sQuery(id+"F2.wireOp",EDGE,"E57.left"),sQuery(id+"F2.wireOp",EDGE,"E57.right"),sQuery(id+"F2.wireOp",EDGE,"98f910ef-10bf-4355-9089-b64edb675ca1.trimOffspring"),sQuery(id+"F2.wireOp",EDGE,"7f1d8590-854d-48a8-a345-113ac86432ce.trimOffspring"),sQuery(id+"F2.wireOp",EDGE,"8eb6f7d6-6f97-4ebc-a51c-8934afb20485.trimOffspring"),sQuery(id+"F2.wireOp",EDGE,"79887d4c-0bb1-4e3d-a504-848fb675985f.trimOffspring"),sQuery(id+"F2.wireOp",EDGE,"6021e146-63f0-49d4-b214-f61fa3b2a401.trimOffspring"),sQuery(id+"F2.wireOp",EDGE,"bdb7ae41-a7ed-46e7-8485-b54428fed669.trimOffspring"),sQuery(id+"F2.wireOp",EDGE,"45a4283d-6044-4d88-b901-0b074d01a6ab.trimOffspring"),sQuery(id+"F2.wireOp",EDGE,"59fc1645-d4a0-4682-934b-e6e005b09d3d.trimOffspring"),sQuery(id+"F2.wireOp",EDGE,"E59.bottom"),sQuery(id+"F2.wireOp",EDGE,"E59.left"),sQuery(id+"F2.wireOp",EDGE,"E60.top"),sQuery(id+"F2.wireOp",EDGE,"E62.bottom"),sQuery(id+"F2.wireOp",EDGE,"E62.top"),sQuery(id+"F2.wireOp",EDGE,"E62.right"),sQuery(id+"F2.wireOp",EDGE,"E63"),sQuery(id+"F2.wireOp",EDGE,"E64"),sQuery(id+"F2.wireOp",EDGE,"E65"),sQuery(id+"F2.wireOp",EDGE,"E66.trimOffspring"),sQuery(id+"F2.wireOp",EDGE,"E67.trimOffspring"),sQuery(id+"F2.wireOp",EDGE,"E68"),sQuery(id+"F2.wireOp",EDGE,"E69"),sQuery(id+"F2.wireOp",EDGE,"E70"),sQuery(id+"F2.wireOp",EDGE,"E72"),sQuery(id+"F2.wireOp",EDGE,"E73.trimOffspring"),sQuery(id+"F2.wireOp",EDGE,"E56.left"),sQuery(id+"F2.wireOp",EDGE,"E74"),sQuery(id+"F2.wireOp",EDGE,"E75.trimOffspring"),sQuery(id+"F2.wireOp",EDGE,"729de1fe-793c-4f06-af17-d50d40598c080.MirrorCS"),sQuery(id+"F2.wireOp",EDGE,"729de1fe-793c-4f06-af17-d50d40598c082.MirrorCS"),sQuery(id+"F2.wireOp",EDGE,"729de1fe-793c-4f06-af17-d50d40598c083.MirrorCS"),sQuery(id+"F2.wireOp",EDGE,"729de1fe-793c-4f06-af17-d50d40598c084.MirrorCS"),sQuery(id+"F2.wireOp",EDGE,"729de1fe-793c-4f06-af17-d50d40598c085.MirrorCS"),sQuery(id+"F2.wireOp",EDGE,"729de1fe-793c-4f06-af17-d50d40598c086.MirrorCS"),sQuery(id+"F2.wireOp",EDGE,"729de1fe-793c-4f06-af17-d50d40598c087.MirrorCS"),sQuery(id+"F2.wireOp",EDGE,"729de1fe-793c-4f06-af17-d50d40598c088.MirrorCS"),sQuery(id+"F2.wireOp",EDGE,"729de1fe-793c-4f06-af17-d50d40598c089.MirrorCS"),sQuery(id+"F2.wireOp",EDGE,"E770.MirrorCS"),sQuery(id+"F2.wireOp",EDGE,"E78.MirrorCS"),sQuery(id+"F2.wireOp",EDGE,"E772.MirrorCS"),sQuery(id+"F2.wireOp",EDGE,"E79.MirrorCS"),sQuery(id+"F2.wireOp",EDGE,"E774.MirrorCS"),sQuery(id+"F2.wireOp",EDGE,"E775.MirrorCS"),sQuery(id+"F2.wireOp",EDGE,"E776.MirrorCS"),sQuery(id+"F2.wireOp",EDGE,"E777.MirrorCS"),sQuery(id+"F2.wireOp",EDGE,"E778.MirrorCS"),sQuery(id+"F2.wireOp",EDGE,"E779.MirrorCS"),sQuery(id+"F2.wireOp",EDGE,"729de1fe-793c-4f06-af17-d50d40598c0820.MirrorCS"),sQuery(id+"F2.wireOp",EDGE,"E80.MirrorCS"),sQuery(id+"F2.wireOp",EDGE,"E82.MirrorCS"),sQuery(id+"F2.wireOp",EDGE,"E83.MirrorCS"),sQuery(id+"F2.wireOp",EDGE,"E84.MirrorCS"),sQuery(id+"F2.wireOp",EDGE,"E85.MirrorCS"),sQuery(id+"F2.wireOp",EDGE,"E86.MirrorCS"),sQuery(id+"F2.wireOp",EDGE,"E92.MirrorCS"),sQuery(id+"F2.wireOp",EDGE,"729de1fe-793c-4f06-af17-d50d40598c0837.MirrorCS"),sQuery(id+"F2.wireOp",EDGE,"729de1fe-793c-4f06-af17-d50d40598c0838.MirrorCS"),sQuery(id+"F2.wireOp",EDGE,"729de1fe-793c-4f06-af17-d50d40598c0841.MirrorCS"),sQuery(id+"F2.wireOp",EDGE,"E95.MirrorCS"),sQuery(id+"F2.wireOp",EDGE,"729de1fe-793c-4f06-af17-d50d40598c0851.MirrorCS"),sQuery(id+"F2.wireOp",EDGE,"E89.MirrorCS"),sQuery(id+"F2.wireOp",EDGE,"E100.MirrorCS"),sQuery(id+"F2.wireOp",EDGE,"E101.MirrorCS"),sQuery(id+"F2.wireOp",EDGE,"E102.MirrorCS"),sQuery(id+"F2.wireOp",EDGE,"E104"),sQuery(id+"F2.wireOp",EDGE,"E105.MirrorCS"),sQuery(id+"F2.wireOp",EDGE,"E106.trimOffspring"),sQuery(id+"F2.wireOp",EDGE,"E108.MirrorCS"),sQuery(id+"F2.wireOp",EDGE,"E109.MirrorCS"),sQuery(id+"F2.wireOp",EDGE,"E110.trimOffspring"),sQuery(id+"F2.wireOp",EDGE,"31b2c9c2-f7eb-4751-8350-943a16306e17.trimOffspring"),sQuery(id+"F2.wireOp",EDGE,"E111.trimOffspring")])],"isStart":false});
            var Q3;
            Q3=makeQuery(id+"F3.opExtrude","CAP_FACE",FACE,{"disambiguationData":[OSD([sQuery(id+"F2.wireOp",EDGE,"E56.bottom"),sQuery(id+"F2.wireOp",EDGE,"E56.top"),sQuery(id+"F2.wireOp",EDGE,"SfhTXy7u-tcII-MEaY-9RSd-v6Q0Sdl2hSPR.bottom"),sQuery(id+"F2.wireOp",EDGE,"SfhTXy7u-tcII-MEaY-9RSd-v6Q0Sdl2hSPR.top"),sQuery(id+"F2.wireOp",EDGE,"SfhTXy7u-tcII-MEaY-9RSd-v6Q0Sdl2hSPR.right"),sQuery(id+"F2.wireOp",EDGE,"RLKNdBM9-fcir-abDg-scLo-AlFl0wZaGOfU.bottom"),sQuery(id+"F2.wireOp",EDGE,"RLKNdBM9-fcir-abDg-scLo-AlFl0wZaGOfU.top"),sQuery(id+"F2.wireOp",EDGE,"RLKNdBM9-fcir-abDg-scLo-AlFl0wZaGOfU.left"),sQuery(id+"F2.wireOp",EDGE,"RLKNdBM9-fcir-abDg-scLo-AlFl0wZaGOfU.right"),sQuery(id+"F2.wireOp",EDGE,"592e8475-5e9e-4e55-86be-326854908ba4.bottom"),sQuery(id+"F2.wireOp",EDGE,"592e8475-5e9e-4e55-86be-326854908ba4.top"),sQuery(id+"F2.wireOp",EDGE,"592e8475-5e9e-4e55-86be-326854908ba4.right"),sQuery(id+"F2.wireOp",EDGE,"E57.bottom"),sQuery(id+"F2.wireOp",EDGE,"E57.top"),sQuery(id+"F2.wireOp",EDGE,"E57.left"),sQuery(id+"F2.wireOp",EDGE,"E57.right"),sQuery(id+"F2.wireOp",EDGE,"98f910ef-10bf-4355-9089-b64edb675ca1.trimOffspring"),sQuery(id+"F2.wireOp",EDGE,"7f1d8590-854d-48a8-a345-113ac86432ce.trimOffspring"),sQuery(id+"F2.wireOp",EDGE,"8eb6f7d6-6f97-4ebc-a51c-8934afb20485.trimOffspring"),sQuery(id+"F2.wireOp",EDGE,"79887d4c-0bb1-4e3d-a504-848fb675985f.trimOffspring"),sQuery(id+"F2.wireOp",EDGE,"6021e146-63f0-49d4-b214-f61fa3b2a401.trimOffspring"),sQuery(id+"F2.wireOp",EDGE,"bdb7ae41-a7ed-46e7-8485-b54428fed669.trimOffspring"),sQuery(id+"F2.wireOp",EDGE,"45a4283d-6044-4d88-b901-0b074d01a6ab.trimOffspring"),sQuery(id+"F2.wireOp",EDGE,"59fc1645-d4a0-4682-934b-e6e005b09d3d.trimOffspring"),sQuery(id+"F2.wireOp",EDGE,"E59.bottom"),sQuery(id+"F2.wireOp",EDGE,"E59.left"),sQuery(id+"F2.wireOp",EDGE,"E60.top"),sQuery(id+"F2.wireOp",EDGE,"E62.bottom"),sQuery(id+"F2.wireOp",EDGE,"E62.top"),sQuery(id+"F2.wireOp",EDGE,"E62.right"),sQuery(id+"F2.wireOp",EDGE,"E63"),sQuery(id+"F2.wireOp",EDGE,"E64"),sQuery(id+"F2.wireOp",EDGE,"E65"),sQuery(id+"F2.wireOp",EDGE,"E66.trimOffspring"),sQuery(id+"F2.wireOp",EDGE,"E67.trimOffspring"),sQuery(id+"F2.wireOp",EDGE,"E68"),sQuery(id+"F2.wireOp",EDGE,"E69"),sQuery(id+"F2.wireOp",EDGE,"E70"),sQuery(id+"F2.wireOp",EDGE,"E72"),sQuery(id+"F2.wireOp",EDGE,"E73.trimOffspring"),sQuery(id+"F2.wireOp",EDGE,"E56.left"),sQuery(id+"F2.wireOp",EDGE,"E74"),sQuery(id+"F2.wireOp",EDGE,"E75.trimOffspring"),sQuery(id+"F2.wireOp",EDGE,"729de1fe-793c-4f06-af17-d50d40598c080.MirrorCS"),sQuery(id+"F2.wireOp",EDGE,"729de1fe-793c-4f06-af17-d50d40598c082.MirrorCS"),sQuery(id+"F2.wireOp",EDGE,"729de1fe-793c-4f06-af17-d50d40598c083.MirrorCS"),sQuery(id+"F2.wireOp",EDGE,"729de1fe-793c-4f06-af17-d50d40598c084.MirrorCS"),sQuery(id+"F2.wireOp",EDGE,"729de1fe-793c-4f06-af17-d50d40598c085.MirrorCS"),sQuery(id+"F2.wireOp",EDGE,"729de1fe-793c-4f06-af17-d50d40598c086.MirrorCS"),sQuery(id+"F2.wireOp",EDGE,"729de1fe-793c-4f06-af17-d50d40598c087.MirrorCS"),sQuery(id+"F2.wireOp",EDGE,"729de1fe-793c-4f06-af17-d50d40598c088.MirrorCS"),sQuery(id+"F2.wireOp",EDGE,"729de1fe-793c-4f06-af17-d50d40598c089.MirrorCS"),sQuery(id+"F2.wireOp",EDGE,"E770.MirrorCS"),sQuery(id+"F2.wireOp",EDGE,"E78.MirrorCS"),sQuery(id+"F2.wireOp",EDGE,"E772.MirrorCS"),sQuery(id+"F2.wireOp",EDGE,"E79.MirrorCS"),sQuery(id+"F2.wireOp",EDGE,"E774.MirrorCS"),sQuery(id+"F2.wireOp",EDGE,"E775.MirrorCS"),sQuery(id+"F2.wireOp",EDGE,"E776.MirrorCS"),sQuery(id+"F2.wireOp",EDGE,"E777.MirrorCS"),sQuery(id+"F2.wireOp",EDGE,"E778.MirrorCS"),sQuery(id+"F2.wireOp",EDGE,"E779.MirrorCS"),sQuery(id+"F2.wireOp",EDGE,"729de1fe-793c-4f06-af17-d50d40598c0820.MirrorCS"),sQuery(id+"F2.wireOp",EDGE,"E80.MirrorCS"),sQuery(id+"F2.wireOp",EDGE,"E82.MirrorCS"),sQuery(id+"F2.wireOp",EDGE,"E83.MirrorCS"),sQuery(id+"F2.wireOp",EDGE,"E84.MirrorCS"),sQuery(id+"F2.wireOp",EDGE,"E85.MirrorCS"),sQuery(id+"F2.wireOp",EDGE,"E86.MirrorCS"),sQuery(id+"F2.wireOp",EDGE,"E92.MirrorCS"),sQuery(id+"F2.wireOp",EDGE,"729de1fe-793c-4f06-af17-d50d40598c0837.MirrorCS"),sQuery(id+"F2.wireOp",EDGE,"729de1fe-793c-4f06-af17-d50d40598c0838.MirrorCS"),sQuery(id+"F2.wireOp",EDGE,"729de1fe-793c-4f06-af17-d50d40598c0841.MirrorCS"),sQuery(id+"F2.wireOp",EDGE,"E95.MirrorCS"),sQuery(id+"F2.wireOp",EDGE,"729de1fe-793c-4f06-af17-d50d40598c0851.MirrorCS"),sQuery(id+"F2.wireOp",EDGE,"E89.MirrorCS"),sQuery(id+"F2.wireOp",EDGE,"E100.MirrorCS"),sQuery(id+"F2.wireOp",EDGE,"E101.MirrorCS"),sQuery(id+"F2.wireOp",EDGE,"E102.MirrorCS"),sQuery(id+"F2.wireOp",EDGE,"E104"),sQuery(id+"F2.wireOp",EDGE,"E105.MirrorCS"),sQuery(id+"F2.wireOp",EDGE,"E106.trimOffspring"),sQuery(id+"F2.wireOp",EDGE,"E108.MirrorCS"),sQuery(id+"F2.wireOp",EDGE,"E109.MirrorCS"),sQuery(id+"F2.wireOp",EDGE,"E110.trimOffspring"),sQuery(id+"F2.wireOp",EDGE,"31b2c9c2-f7eb-4751-8350-943a16306e17.trimOffspring"),sQuery(id+"F2.wireOp",EDGE,"E111.trimOffspring")])],"isStart":true});
            var Q4;
            Q4=makeQuery(id+"F3.opExtrude","SWEPT_FACE",FACE,{"disambiguationData":[OSD([sQuery(id+"F2.wireOp",EDGE,"E59.bottom")])]});
            var Q5;
            Q5=makeQuery(id+"F3.opExtrude","SWEPT_FACE",FACE,{"disambiguationData":[OSD([sQuery(id+"F2.wireOp",EDGE,"E74")])]});
            var Q6;
            Q6=makeQuery(id+"F3.opExtrude","SWEPT_FACE",FACE,{"disambiguationData":[OSD([sQuery(id+"F2.wireOp",EDGE,"E62.top")])]});
            var Q7;
            Q7=makeQuery(id+"F3.opExtrude","SWEPT_FACE",FACE,{"disambiguationData":[OSD([sQuery(id+"F2.wireOp",EDGE,"E60.top")])]});
            var Q8;
            Q8=makeQuery(id+"F3.opExtrude","SWEPT_FACE",FACE,{"disambiguationData":[OSD([sQuery(id+"F2.wireOp",EDGE,"E62.bottom")])]});
            var Q9;
            Q9=makeQuery(id+"F3.opExtrude","SWEPT_FACE",FACE,{"disambiguationData":[OSD([sQuery(id+"F2.wireOp",EDGE,"E63")])]});
            var Q10;
            Q10=makeQuery(id+"F3.opExtrude","SWEPT_FACE",FACE,{"disambiguationData":[OSD([sQuery(id+"F2.wireOp",EDGE,"E65")])]});
            var Q11;
            Q11=makeQuery(id+"F3.opExtrude","SWEPT_FACE",FACE,{"disambiguationData":[OSD([sQuery(id+"F2.wireOp",EDGE,"E64")])]});
            booleanBodies(context, id + "F4", {"operationType" : BooleanOperationType.SUBTRACTION, "tools" : qUnion([Q0]), "targets" : qUnion([Q1]), "offset" : true, "entitiesToOffset" : qUnion([Q2, Q3, Q4, Q5, Q6, Q7, Q8, Q9, Q10, Q11]), "offsetDistance" : 0.6 * mm, "keepTools" : true});
        }
        {
            var Q0;
            Q0=makeQuery(id+"F3.opExtrude","SWEPT_BODY",BODY,{"disambiguationData":[OSD([sQuery(id+"F2.wireOp",EDGE,"E56.bottom"),sQuery(id+"F2.wireOp",EDGE,"E56.top"),sQuery(id+"F2.wireOp",EDGE,"SfhTXy7u-tcII-MEaY-9RSd-v6Q0Sdl2hSPR.bottom"),sQuery(id+"F2.wireOp",EDGE,"SfhTXy7u-tcII-MEaY-9RSd-v6Q0Sdl2hSPR.top"),sQuery(id+"F2.wireOp",EDGE,"SfhTXy7u-tcII-MEaY-9RSd-v6Q0Sdl2hSPR.right"),sQuery(id+"F2.wireOp",EDGE,"RLKNdBM9-fcir-abDg-scLo-AlFl0wZaGOfU.bottom"),sQuery(id+"F2.wireOp",EDGE,"RLKNdBM9-fcir-abDg-scLo-AlFl0wZaGOfU.top"),sQuery(id+"F2.wireOp",EDGE,"RLKNdBM9-fcir-abDg-scLo-AlFl0wZaGOfU.left"),sQuery(id+"F2.wireOp",EDGE,"RLKNdBM9-fcir-abDg-scLo-AlFl0wZaGOfU.right"),sQuery(id+"F2.wireOp",EDGE,"592e8475-5e9e-4e55-86be-326854908ba4.bottom"),sQuery(id+"F2.wireOp",EDGE,"592e8475-5e9e-4e55-86be-326854908ba4.top"),sQuery(id+"F2.wireOp",EDGE,"592e8475-5e9e-4e55-86be-326854908ba4.right"),sQuery(id+"F2.wireOp",EDGE,"E57.bottom"),sQuery(id+"F2.wireOp",EDGE,"E57.top"),sQuery(id+"F2.wireOp",EDGE,"E57.left"),sQuery(id+"F2.wireOp",EDGE,"E57.right"),sQuery(id+"F2.wireOp",EDGE,"98f910ef-10bf-4355-9089-b64edb675ca1.trimOffspring"),sQuery(id+"F2.wireOp",EDGE,"7f1d8590-854d-48a8-a345-113ac86432ce.trimOffspring"),sQuery(id+"F2.wireOp",EDGE,"8eb6f7d6-6f97-4ebc-a51c-8934afb20485.trimOffspring"),sQuery(id+"F2.wireOp",EDGE,"79887d4c-0bb1-4e3d-a504-848fb675985f.trimOffspring"),sQuery(id+"F2.wireOp",EDGE,"6021e146-63f0-49d4-b214-f61fa3b2a401.trimOffspring"),sQuery(id+"F2.wireOp",EDGE,"bdb7ae41-a7ed-46e7-8485-b54428fed669.trimOffspring"),sQuery(id+"F2.wireOp",EDGE,"45a4283d-6044-4d88-b901-0b074d01a6ab.trimOffspring"),sQuery(id+"F2.wireOp",EDGE,"59fc1645-d4a0-4682-934b-e6e005b09d3d.trimOffspring"),sQuery(id+"F2.wireOp",EDGE,"E59.bottom"),sQuery(id+"F2.wireOp",EDGE,"E59.left"),sQuery(id+"F2.wireOp",EDGE,"E60.top"),sQuery(id+"F2.wireOp",EDGE,"E62.bottom"),sQuery(id+"F2.wireOp",EDGE,"E62.top"),sQuery(id+"F2.wireOp",EDGE,"E62.right"),sQuery(id+"F2.wireOp",EDGE,"E63"),sQuery(id+"F2.wireOp",EDGE,"E64"),sQuery(id+"F2.wireOp",EDGE,"E65"),sQuery(id+"F2.wireOp",EDGE,"E66.trimOffspring"),sQuery(id+"F2.wireOp",EDGE,"E67.trimOffspring"),sQuery(id+"F2.wireOp",EDGE,"E68"),sQuery(id+"F2.wireOp",EDGE,"E69"),sQuery(id+"F2.wireOp",EDGE,"E70"),sQuery(id+"F2.wireOp",EDGE,"E72"),sQuery(id+"F2.wireOp",EDGE,"E73.trimOffspring"),sQuery(id+"F2.wireOp",EDGE,"E56.left"),sQuery(id+"F2.wireOp",EDGE,"E74"),sQuery(id+"F2.wireOp",EDGE,"E75.trimOffspring"),sQuery(id+"F2.wireOp",EDGE,"729de1fe-793c-4f06-af17-d50d40598c080.MirrorCS"),sQuery(id+"F2.wireOp",EDGE,"729de1fe-793c-4f06-af17-d50d40598c082.MirrorCS"),sQuery(id+"F2.wireOp",EDGE,"729de1fe-793c-4f06-af17-d50d40598c083.MirrorCS"),sQuery(id+"F2.wireOp",EDGE,"729de1fe-793c-4f06-af17-d50d40598c084.MirrorCS"),sQuery(id+"F2.wireOp",EDGE,"729de1fe-793c-4f06-af17-d50d40598c085.MirrorCS"),sQuery(id+"F2.wireOp",EDGE,"729de1fe-793c-4f06-af17-d50d40598c086.MirrorCS"),sQuery(id+"F2.wireOp",EDGE,"729de1fe-793c-4f06-af17-d50d40598c087.MirrorCS"),sQuery(id+"F2.wireOp",EDGE,"729de1fe-793c-4f06-af17-d50d40598c088.MirrorCS"),sQuery(id+"F2.wireOp",EDGE,"729de1fe-793c-4f06-af17-d50d40598c089.MirrorCS"),sQuery(id+"F2.wireOp",EDGE,"E770.MirrorCS"),sQuery(id+"F2.wireOp",EDGE,"E78.MirrorCS"),sQuery(id+"F2.wireOp",EDGE,"E772.MirrorCS"),sQuery(id+"F2.wireOp",EDGE,"E79.MirrorCS"),sQuery(id+"F2.wireOp",EDGE,"E774.MirrorCS"),sQuery(id+"F2.wireOp",EDGE,"E775.MirrorCS"),sQuery(id+"F2.wireOp",EDGE,"E776.MirrorCS"),sQuery(id+"F2.wireOp",EDGE,"E777.MirrorCS"),sQuery(id+"F2.wireOp",EDGE,"E778.MirrorCS"),sQuery(id+"F2.wireOp",EDGE,"E779.MirrorCS"),sQuery(id+"F2.wireOp",EDGE,"729de1fe-793c-4f06-af17-d50d40598c0820.MirrorCS"),sQuery(id+"F2.wireOp",EDGE,"E80.MirrorCS"),sQuery(id+"F2.wireOp",EDGE,"E82.MirrorCS"),sQuery(id+"F2.wireOp",EDGE,"E83.MirrorCS"),sQuery(id+"F2.wireOp",EDGE,"E84.MirrorCS"),sQuery(id+"F2.wireOp",EDGE,"E85.MirrorCS"),sQuery(id+"F2.wireOp",EDGE,"E86.MirrorCS"),sQuery(id+"F2.wireOp",EDGE,"E92.MirrorCS"),sQuery(id+"F2.wireOp",EDGE,"729de1fe-793c-4f06-af17-d50d40598c0837.MirrorCS"),sQuery(id+"F2.wireOp",EDGE,"729de1fe-793c-4f06-af17-d50d40598c0838.MirrorCS"),sQuery(id+"F2.wireOp",EDGE,"729de1fe-793c-4f06-af17-d50d40598c0841.MirrorCS"),sQuery(id+"F2.wireOp",EDGE,"E95.MirrorCS"),sQuery(id+"F2.wireOp",EDGE,"729de1fe-793c-4f06-af17-d50d40598c0851.MirrorCS"),sQuery(id+"F2.wireOp",EDGE,"E89.MirrorCS"),sQuery(id+"F2.wireOp",EDGE,"E100.MirrorCS"),sQuery(id+"F2.wireOp",EDGE,"E101.MirrorCS"),sQuery(id+"F2.wireOp",EDGE,"E102.MirrorCS"),sQuery(id+"F2.wireOp",EDGE,"E104"),sQuery(id+"F2.wireOp",EDGE,"E105.MirrorCS"),sQuery(id+"F2.wireOp",EDGE,"E106.trimOffspring"),sQuery(id+"F2.wireOp",EDGE,"E108.MirrorCS"),sQuery(id+"F2.wireOp",EDGE,"E109.MirrorCS"),sQuery(id+"F2.wireOp",EDGE,"E110.trimOffspring"),sQuery(id+"F2.wireOp",EDGE,"31b2c9c2-f7eb-4751-8350-943a16306e17.trimOffspring"),sQuery(id+"F2.wireOp",EDGE,"E111.trimOffspring")])]});
            transform(context, id + "F5", {"entities" : qUnion([Q0]), "transformType" : TransformType.TRANSLATION_3D, "dx" : 0 * mm, "dy" : -338.7 * mm, "dz" : 0 * mm, "makeCopy" : true});
        }
        {
            var Q0;
            Q0=makeQuery(id+"F5.opPattern","COPY",BODY,{"derivedFrom":makeQuery(id+"F3.opExtrude","SWEPT_BODY",BODY,{"disambiguationData":[OSD([sQuery(id+"F2.wireOp",EDGE,"E56.bottom"),sQuery(id+"F2.wireOp",EDGE,"E56.top"),sQuery(id+"F2.wireOp",EDGE,"SfhTXy7u-tcII-MEaY-9RSd-v6Q0Sdl2hSPR.bottom"),sQuery(id+"F2.wireOp",EDGE,"SfhTXy7u-tcII-MEaY-9RSd-v6Q0Sdl2hSPR.top"),sQuery(id+"F2.wireOp",EDGE,"SfhTXy7u-tcII-MEaY-9RSd-v6Q0Sdl2hSPR.right"),sQuery(id+"F2.wireOp",EDGE,"RLKNdBM9-fcir-abDg-scLo-AlFl0wZaGOfU.bottom"),sQuery(id+"F2.wireOp",EDGE,"RLKNdBM9-fcir-abDg-scLo-AlFl0wZaGOfU.top"),sQuery(id+"F2.wireOp",EDGE,"RLKNdBM9-fcir-abDg-scLo-AlFl0wZaGOfU.left"),sQuery(id+"F2.wireOp",EDGE,"RLKNdBM9-fcir-abDg-scLo-AlFl0wZaGOfU.right"),sQuery(id+"F2.wireOp",EDGE,"592e8475-5e9e-4e55-86be-326854908ba4.bottom"),sQuery(id+"F2.wireOp",EDGE,"592e8475-5e9e-4e55-86be-326854908ba4.top"),sQuery(id+"F2.wireOp",EDGE,"592e8475-5e9e-4e55-86be-326854908ba4.right"),sQuery(id+"F2.wireOp",EDGE,"E57.bottom"),sQuery(id+"F2.wireOp",EDGE,"E57.top"),sQuery(id+"F2.wireOp",EDGE,"E57.left"),sQuery(id+"F2.wireOp",EDGE,"E57.right"),sQuery(id+"F2.wireOp",EDGE,"98f910ef-10bf-4355-9089-b64edb675ca1.trimOffspring"),sQuery(id+"F2.wireOp",EDGE,"7f1d8590-854d-48a8-a345-113ac86432ce.trimOffspring"),sQuery(id+"F2.wireOp",EDGE,"8eb6f7d6-6f97-4ebc-a51c-8934afb20485.trimOffspring"),sQuery(id+"F2.wireOp",EDGE,"79887d4c-0bb1-4e3d-a504-848fb675985f.trimOffspring"),sQuery(id+"F2.wireOp",EDGE,"6021e146-63f0-49d4-b214-f61fa3b2a401.trimOffspring"),sQuery(id+"F2.wireOp",EDGE,"bdb7ae41-a7ed-46e7-8485-b54428fed669.trimOffspring"),sQuery(id+"F2.wireOp",EDGE,"45a4283d-6044-4d88-b901-0b074d01a6ab.trimOffspring"),sQuery(id+"F2.wireOp",EDGE,"59fc1645-d4a0-4682-934b-e6e005b09d3d.trimOffspring"),sQuery(id+"F2.wireOp",EDGE,"E59.bottom"),sQuery(id+"F2.wireOp",EDGE,"E59.left"),sQuery(id+"F2.wireOp",EDGE,"E60.top"),sQuery(id+"F2.wireOp",EDGE,"E62.bottom"),sQuery(id+"F2.wireOp",EDGE,"E62.top"),sQuery(id+"F2.wireOp",EDGE,"E62.right"),sQuery(id+"F2.wireOp",EDGE,"E63"),sQuery(id+"F2.wireOp",EDGE,"E64"),sQuery(id+"F2.wireOp",EDGE,"E65"),sQuery(id+"F2.wireOp",EDGE,"E66.trimOffspring"),sQuery(id+"F2.wireOp",EDGE,"E67.trimOffspring"),sQuery(id+"F2.wireOp",EDGE,"E68"),sQuery(id+"F2.wireOp",EDGE,"E69"),sQuery(id+"F2.wireOp",EDGE,"E70"),sQuery(id+"F2.wireOp",EDGE,"E72"),sQuery(id+"F2.wireOp",EDGE,"E73.trimOffspring"),sQuery(id+"F2.wireOp",EDGE,"E56.left"),sQuery(id+"F2.wireOp",EDGE,"E74"),sQuery(id+"F2.wireOp",EDGE,"E75.trimOffspring"),sQuery(id+"F2.wireOp",EDGE,"729de1fe-793c-4f06-af17-d50d40598c080.MirrorCS"),sQuery(id+"F2.wireOp",EDGE,"729de1fe-793c-4f06-af17-d50d40598c082.MirrorCS"),sQuery(id+"F2.wireOp",EDGE,"729de1fe-793c-4f06-af17-d50d40598c083.MirrorCS"),sQuery(id+"F2.wireOp",EDGE,"729de1fe-793c-4f06-af17-d50d40598c084.MirrorCS"),sQuery(id+"F2.wireOp",EDGE,"729de1fe-793c-4f06-af17-d50d40598c085.MirrorCS"),sQuery(id+"F2.wireOp",EDGE,"729de1fe-793c-4f06-af17-d50d40598c086.MirrorCS"),sQuery(id+"F2.wireOp",EDGE,"729de1fe-793c-4f06-af17-d50d40598c087.MirrorCS"),sQuery(id+"F2.wireOp",EDGE,"729de1fe-793c-4f06-af17-d50d40598c088.MirrorCS"),sQuery(id+"F2.wireOp",EDGE,"729de1fe-793c-4f06-af17-d50d40598c089.MirrorCS"),sQuery(id+"F2.wireOp",EDGE,"E770.MirrorCS"),sQuery(id+"F2.wireOp",EDGE,"E78.MirrorCS"),sQuery(id+"F2.wireOp",EDGE,"E772.MirrorCS"),sQuery(id+"F2.wireOp",EDGE,"E79.MirrorCS"),sQuery(id+"F2.wireOp",EDGE,"E774.MirrorCS"),sQuery(id+"F2.wireOp",EDGE,"E775.MirrorCS"),sQuery(id+"F2.wireOp",EDGE,"E776.MirrorCS"),sQuery(id+"F2.wireOp",EDGE,"E777.MirrorCS"),sQuery(id+"F2.wireOp",EDGE,"E778.MirrorCS"),sQuery(id+"F2.wireOp",EDGE,"E779.MirrorCS"),sQuery(id+"F2.wireOp",EDGE,"729de1fe-793c-4f06-af17-d50d40598c0820.MirrorCS"),sQuery(id+"F2.wireOp",EDGE,"E80.MirrorCS"),sQuery(id+"F2.wireOp",EDGE,"E82.MirrorCS"),sQuery(id+"F2.wireOp",EDGE,"E83.MirrorCS"),sQuery(id+"F2.wireOp",EDGE,"E84.MirrorCS"),sQuery(id+"F2.wireOp",EDGE,"E85.MirrorCS"),sQuery(id+"F2.wireOp",EDGE,"E86.MirrorCS"),sQuery(id+"F2.wireOp",EDGE,"E92.MirrorCS"),sQuery(id+"F2.wireOp",EDGE,"729de1fe-793c-4f06-af17-d50d40598c0837.MirrorCS"),sQuery(id+"F2.wireOp",EDGE,"729de1fe-793c-4f06-af17-d50d40598c0838.MirrorCS"),sQuery(id+"F2.wireOp",EDGE,"729de1fe-793c-4f06-af17-d50d40598c0841.MirrorCS"),sQuery(id+"F2.wireOp",EDGE,"E95.MirrorCS"),sQuery(id+"F2.wireOp",EDGE,"729de1fe-793c-4f06-af17-d50d40598c0851.MirrorCS"),sQuery(id+"F2.wireOp",EDGE,"E89.MirrorCS"),sQuery(id+"F2.wireOp",EDGE,"E100.MirrorCS"),sQuery(id+"F2.wireOp",EDGE,"E101.MirrorCS"),sQuery(id+"F2.wireOp",EDGE,"E102.MirrorCS"),sQuery(id+"F2.wireOp",EDGE,"E104"),sQuery(id+"F2.wireOp",EDGE,"E105.MirrorCS"),sQuery(id+"F2.wireOp",EDGE,"E106.trimOffspring"),sQuery(id+"F2.wireOp",EDGE,"E108.MirrorCS"),sQuery(id+"F2.wireOp",EDGE,"E109.MirrorCS"),sQuery(id+"F2.wireOp",EDGE,"E110.trimOffspring"),sQuery(id+"F2.wireOp",EDGE,"31b2c9c2-f7eb-4751-8350-943a16306e17.trimOffspring"),sQuery(id+"F2.wireOp",EDGE,"E111.trimOffspring")])]}),"instanceName":"1"});
            var Q1;
            Q1=makeQuery(id+"F1.opExtrude","SWEPT_BODY",BODY,{"disambiguationData":[OSD([sQuery(id+"F0.wireOp",EDGE,"E0.bottom"),sQuery(id+"F0.wireOp",EDGE,"E0.top"),sQuery(id+"F0.wireOp",EDGE,"E0.left"),sQuery(id+"F0.wireOp",EDGE,"E0.right"),sQuery(id+"F0.wireOp",EDGE,"E3.trimOffspring"),sQuery(id+"F0.wireOp",EDGE,"E6.bottom"),sQuery(id+"F0.wireOp",EDGE,"E6.top"),sQuery(id+"F0.wireOp",EDGE,"E6.left"),sQuery(id+"F0.wireOp",EDGE,"E6.right"),sQuery(id+"F0.wireOp",EDGE,"E7.bottom"),sQuery(id+"F0.wireOp",EDGE,"E7.top"),sQuery(id+"F0.wireOp",EDGE,"E7.left"),sQuery(id+"F0.wireOp",EDGE,"E7.right"),sQuery(id+"F0.wireOp",EDGE,"1BBTkZs5-luX3-xtZO-tfno-nD7ZldyCOrRv"),sQuery(id+"F0.wireOp",EDGE,"E13.MirrorCS"),sQuery(id+"F0.wireOp",EDGE,"E14.MirrorCS"),sQuery(id+"F0.wireOp",EDGE,"E10.MirrorCS"),sQuery(id+"F0.wireOp",EDGE,"E15.MirrorCS"),sQuery(id+"F0.wireOp",EDGE,"edba22f7-fcec-4b76-9e19-08ec19d2e6a00.MirrorC"),sQuery(id+"F0.wireOp",EDGE,"E16.MirrorCS"),sQuery(id+"F0.wireOp",EDGE,"E17.MirrorCS"),sQuery(id+"F0.wireOp",EDGE,"E20.MirrorCS"),sQuery(id+"F0.wireOp",EDGE,"E21.MirrorCS"),sQuery(id+"F0.wireOp",EDGE,"E26.MirrorCS"),sQuery(id+"F0.wireOp",EDGE,"E27.MirrorCS"),sQuery(id+"F0.wireOp",EDGE,"E28.MirrorCS"),sQuery(id+"F0.wireOp",EDGE,"E29.MirrorCS"),sQuery(id+"F0.wireOp",EDGE,"e9cac41d-f357-42ad-afaa-485d0ff043840.MirrorC"),sQuery(id+"F0.wireOp",EDGE,"E30.MirrorCS"),sQuery(id+"F0.wireOp",EDGE,"E31.MirrorCS"),sQuery(id+"F0.wireOp",EDGE,"E32.MirrorCS"),sQuery(id+"F0.wireOp",EDGE,"E33.MirrorCS"),sQuery(id+"F0.wireOp",EDGE,"E34.MirrorCS"),sQuery(id+"F0.wireOp",EDGE,"E35.MirrorCS"),sQuery(id+"F0.wireOp",EDGE,"E36.MirrorCS"),sQuery(id+"F0.wireOp",EDGE,"E37.MirrorCS"),sQuery(id+"F0.wireOp",EDGE,"f40b6c40-3a45-4a40-b477-66a71d50dfa00.MirrorC"),sQuery(id+"F0.wireOp",EDGE,"E38.MirrorCS"),sQuery(id+"F0.wireOp",EDGE,"E39.MirrorCS"),sQuery(id+"F0.wireOp",EDGE,"E40.MirrorCS"),sQuery(id+"F0.wireOp",EDGE,"E41.MirrorCS"),sQuery(id+"F0.wireOp",EDGE,"E44.left"),sQuery(id+"F0.wireOp",EDGE,"E44.right"),sQuery(id+"F0.wireOp",EDGE,"eyhBYY9M-95YG-LpN2-QZ7T-SWmW0xq0itgo")])]});
            var Q2;
            Q2=makeQuery(id+"F5.opPattern","COPY",FACE,{"derivedFrom":makeQuery(id+"F3.opExtrude","CAP_FACE",FACE,{"disambiguationData":[OSD([sQuery(id+"F2.wireOp",EDGE,"E56.bottom"),sQuery(id+"F2.wireOp",EDGE,"E56.top"),sQuery(id+"F2.wireOp",EDGE,"SfhTXy7u-tcII-MEaY-9RSd-v6Q0Sdl2hSPR.bottom"),sQuery(id+"F2.wireOp",EDGE,"SfhTXy7u-tcII-MEaY-9RSd-v6Q0Sdl2hSPR.top"),sQuery(id+"F2.wireOp",EDGE,"SfhTXy7u-tcII-MEaY-9RSd-v6Q0Sdl2hSPR.right"),sQuery(id+"F2.wireOp",EDGE,"RLKNdBM9-fcir-abDg-scLo-AlFl0wZaGOfU.bottom"),sQuery(id+"F2.wireOp",EDGE,"RLKNdBM9-fcir-abDg-scLo-AlFl0wZaGOfU.top"),sQuery(id+"F2.wireOp",EDGE,"RLKNdBM9-fcir-abDg-scLo-AlFl0wZaGOfU.left"),sQuery(id+"F2.wireOp",EDGE,"RLKNdBM9-fcir-abDg-scLo-AlFl0wZaGOfU.right"),sQuery(id+"F2.wireOp",EDGE,"592e8475-5e9e-4e55-86be-326854908ba4.bottom"),sQuery(id+"F2.wireOp",EDGE,"592e8475-5e9e-4e55-86be-326854908ba4.top"),sQuery(id+"F2.wireOp",EDGE,"592e8475-5e9e-4e55-86be-326854908ba4.right"),sQuery(id+"F2.wireOp",EDGE,"E57.bottom"),sQuery(id+"F2.wireOp",EDGE,"E57.top"),sQuery(id+"F2.wireOp",EDGE,"E57.left"),sQuery(id+"F2.wireOp",EDGE,"E57.right"),sQuery(id+"F2.wireOp",EDGE,"98f910ef-10bf-4355-9089-b64edb675ca1.trimOffspring"),sQuery(id+"F2.wireOp",EDGE,"7f1d8590-854d-48a8-a345-113ac86432ce.trimOffspring"),sQuery(id+"F2.wireOp",EDGE,"8eb6f7d6-6f97-4ebc-a51c-8934afb20485.trimOffspring"),sQuery(id+"F2.wireOp",EDGE,"79887d4c-0bb1-4e3d-a504-848fb675985f.trimOffspring"),sQuery(id+"F2.wireOp",EDGE,"6021e146-63f0-49d4-b214-f61fa3b2a401.trimOffspring"),sQuery(id+"F2.wireOp",EDGE,"bdb7ae41-a7ed-46e7-8485-b54428fed669.trimOffspring"),sQuery(id+"F2.wireOp",EDGE,"45a4283d-6044-4d88-b901-0b074d01a6ab.trimOffspring"),sQuery(id+"F2.wireOp",EDGE,"59fc1645-d4a0-4682-934b-e6e005b09d3d.trimOffspring"),sQuery(id+"F2.wireOp",EDGE,"E59.bottom"),sQuery(id+"F2.wireOp",EDGE,"E59.left"),sQuery(id+"F2.wireOp",EDGE,"E60.top"),sQuery(id+"F2.wireOp",EDGE,"E62.bottom"),sQuery(id+"F2.wireOp",EDGE,"E62.top"),sQuery(id+"F2.wireOp",EDGE,"E62.right"),sQuery(id+"F2.wireOp",EDGE,"E63"),sQuery(id+"F2.wireOp",EDGE,"E64"),sQuery(id+"F2.wireOp",EDGE,"E65"),sQuery(id+"F2.wireOp",EDGE,"E66.trimOffspring"),sQuery(id+"F2.wireOp",EDGE,"E67.trimOffspring"),sQuery(id+"F2.wireOp",EDGE,"E68"),sQuery(id+"F2.wireOp",EDGE,"E69"),sQuery(id+"F2.wireOp",EDGE,"E70"),sQuery(id+"F2.wireOp",EDGE,"E72"),sQuery(id+"F2.wireOp",EDGE,"E73.trimOffspring"),sQuery(id+"F2.wireOp",EDGE,"E56.left"),sQuery(id+"F2.wireOp",EDGE,"E74"),sQuery(id+"F2.wireOp",EDGE,"E75.trimOffspring"),sQuery(id+"F2.wireOp",EDGE,"729de1fe-793c-4f06-af17-d50d40598c080.MirrorCS"),sQuery(id+"F2.wireOp",EDGE,"729de1fe-793c-4f06-af17-d50d40598c082.MirrorCS"),sQuery(id+"F2.wireOp",EDGE,"729de1fe-793c-4f06-af17-d50d40598c083.MirrorCS"),sQuery(id+"F2.wireOp",EDGE,"729de1fe-793c-4f06-af17-d50d40598c084.MirrorCS"),sQuery(id+"F2.wireOp",EDGE,"729de1fe-793c-4f06-af17-d50d40598c085.MirrorCS"),sQuery(id+"F2.wireOp",EDGE,"729de1fe-793c-4f06-af17-d50d40598c086.MirrorCS"),sQuery(id+"F2.wireOp",EDGE,"729de1fe-793c-4f06-af17-d50d40598c087.MirrorCS"),sQuery(id+"F2.wireOp",EDGE,"729de1fe-793c-4f06-af17-d50d40598c088.MirrorCS"),sQuery(id+"F2.wireOp",EDGE,"729de1fe-793c-4f06-af17-d50d40598c089.MirrorCS"),sQuery(id+"F2.wireOp",EDGE,"E770.MirrorCS"),sQuery(id+"F2.wireOp",EDGE,"E78.MirrorCS"),sQuery(id+"F2.wireOp",EDGE,"E772.MirrorCS"),sQuery(id+"F2.wireOp",EDGE,"E79.MirrorCS"),sQuery(id+"F2.wireOp",EDGE,"E774.MirrorCS"),sQuery(id+"F2.wireOp",EDGE,"E775.MirrorCS"),sQuery(id+"F2.wireOp",EDGE,"E776.MirrorCS"),sQuery(id+"F2.wireOp",EDGE,"E777.MirrorCS"),sQuery(id+"F2.wireOp",EDGE,"E778.MirrorCS"),sQuery(id+"F2.wireOp",EDGE,"E779.MirrorCS"),sQuery(id+"F2.wireOp",EDGE,"729de1fe-793c-4f06-af17-d50d40598c0820.MirrorCS"),sQuery(id+"F2.wireOp",EDGE,"E80.MirrorCS"),sQuery(id+"F2.wireOp",EDGE,"E82.MirrorCS"),sQuery(id+"F2.wireOp",EDGE,"E83.MirrorCS"),sQuery(id+"F2.wireOp",EDGE,"E84.MirrorCS"),sQuery(id+"F2.wireOp",EDGE,"E85.MirrorCS"),sQuery(id+"F2.wireOp",EDGE,"E86.MirrorCS"),sQuery(id+"F2.wireOp",EDGE,"E92.MirrorCS"),sQuery(id+"F2.wireOp",EDGE,"729de1fe-793c-4f06-af17-d50d40598c0837.MirrorCS"),sQuery(id+"F2.wireOp",EDGE,"729de1fe-793c-4f06-af17-d50d40598c0838.MirrorCS"),sQuery(id+"F2.wireOp",EDGE,"729de1fe-793c-4f06-af17-d50d40598c0841.MirrorCS"),sQuery(id+"F2.wireOp",EDGE,"E95.MirrorCS"),sQuery(id+"F2.wireOp",EDGE,"729de1fe-793c-4f06-af17-d50d40598c0851.MirrorCS"),sQuery(id+"F2.wireOp",EDGE,"E89.MirrorCS"),sQuery(id+"F2.wireOp",EDGE,"E100.MirrorCS"),sQuery(id+"F2.wireOp",EDGE,"E101.MirrorCS"),sQuery(id+"F2.wireOp",EDGE,"E102.MirrorCS"),sQuery(id+"F2.wireOp",EDGE,"E104"),sQuery(id+"F2.wireOp",EDGE,"E105.MirrorCS"),sQuery(id+"F2.wireOp",EDGE,"E106.trimOffspring"),sQuery(id+"F2.wireOp",EDGE,"E108.MirrorCS"),sQuery(id+"F2.wireOp",EDGE,"E109.MirrorCS"),sQuery(id+"F2.wireOp",EDGE,"E110.trimOffspring"),sQuery(id+"F2.wireOp",EDGE,"31b2c9c2-f7eb-4751-8350-943a16306e17.trimOffspring"),sQuery(id+"F2.wireOp",EDGE,"E111.trimOffspring")])],"isStart":true}),"instanceName":"1"});
            var Q3;
            Q3=makeQuery(id+"F5.opPattern","COPY",FACE,{"derivedFrom":makeQuery(id+"F3.opExtrude","CAP_FACE",FACE,{"disambiguationData":[OSD([sQuery(id+"F2.wireOp",EDGE,"E56.bottom"),sQuery(id+"F2.wireOp",EDGE,"E56.top"),sQuery(id+"F2.wireOp",EDGE,"SfhTXy7u-tcII-MEaY-9RSd-v6Q0Sdl2hSPR.bottom"),sQuery(id+"F2.wireOp",EDGE,"SfhTXy7u-tcII-MEaY-9RSd-v6Q0Sdl2hSPR.top"),sQuery(id+"F2.wireOp",EDGE,"SfhTXy7u-tcII-MEaY-9RSd-v6Q0Sdl2hSPR.right"),sQuery(id+"F2.wireOp",EDGE,"RLKNdBM9-fcir-abDg-scLo-AlFl0wZaGOfU.bottom"),sQuery(id+"F2.wireOp",EDGE,"RLKNdBM9-fcir-abDg-scLo-AlFl0wZaGOfU.top"),sQuery(id+"F2.wireOp",EDGE,"RLKNdBM9-fcir-abDg-scLo-AlFl0wZaGOfU.left"),sQuery(id+"F2.wireOp",EDGE,"RLKNdBM9-fcir-abDg-scLo-AlFl0wZaGOfU.right"),sQuery(id+"F2.wireOp",EDGE,"592e8475-5e9e-4e55-86be-326854908ba4.bottom"),sQuery(id+"F2.wireOp",EDGE,"592e8475-5e9e-4e55-86be-326854908ba4.top"),sQuery(id+"F2.wireOp",EDGE,"592e8475-5e9e-4e55-86be-326854908ba4.right"),sQuery(id+"F2.wireOp",EDGE,"E57.bottom"),sQuery(id+"F2.wireOp",EDGE,"E57.top"),sQuery(id+"F2.wireOp",EDGE,"E57.left"),sQuery(id+"F2.wireOp",EDGE,"E57.right"),sQuery(id+"F2.wireOp",EDGE,"98f910ef-10bf-4355-9089-b64edb675ca1.trimOffspring"),sQuery(id+"F2.wireOp",EDGE,"7f1d8590-854d-48a8-a345-113ac86432ce.trimOffspring"),sQuery(id+"F2.wireOp",EDGE,"8eb6f7d6-6f97-4ebc-a51c-8934afb20485.trimOffspring"),sQuery(id+"F2.wireOp",EDGE,"79887d4c-0bb1-4e3d-a504-848fb675985f.trimOffspring"),sQuery(id+"F2.wireOp",EDGE,"6021e146-63f0-49d4-b214-f61fa3b2a401.trimOffspring"),sQuery(id+"F2.wireOp",EDGE,"bdb7ae41-a7ed-46e7-8485-b54428fed669.trimOffspring"),sQuery(id+"F2.wireOp",EDGE,"45a4283d-6044-4d88-b901-0b074d01a6ab.trimOffspring"),sQuery(id+"F2.wireOp",EDGE,"59fc1645-d4a0-4682-934b-e6e005b09d3d.trimOffspring"),sQuery(id+"F2.wireOp",EDGE,"E59.bottom"),sQuery(id+"F2.wireOp",EDGE,"E59.left"),sQuery(id+"F2.wireOp",EDGE,"E60.top"),sQuery(id+"F2.wireOp",EDGE,"E62.bottom"),sQuery(id+"F2.wireOp",EDGE,"E62.top"),sQuery(id+"F2.wireOp",EDGE,"E62.right"),sQuery(id+"F2.wireOp",EDGE,"E63"),sQuery(id+"F2.wireOp",EDGE,"E64"),sQuery(id+"F2.wireOp",EDGE,"E65"),sQuery(id+"F2.wireOp",EDGE,"E66.trimOffspring"),sQuery(id+"F2.wireOp",EDGE,"E67.trimOffspring"),sQuery(id+"F2.wireOp",EDGE,"E68"),sQuery(id+"F2.wireOp",EDGE,"E69"),sQuery(id+"F2.wireOp",EDGE,"E70"),sQuery(id+"F2.wireOp",EDGE,"E72"),sQuery(id+"F2.wireOp",EDGE,"E73.trimOffspring"),sQuery(id+"F2.wireOp",EDGE,"E56.left"),sQuery(id+"F2.wireOp",EDGE,"E74"),sQuery(id+"F2.wireOp",EDGE,"E75.trimOffspring"),sQuery(id+"F2.wireOp",EDGE,"729de1fe-793c-4f06-af17-d50d40598c080.MirrorCS"),sQuery(id+"F2.wireOp",EDGE,"729de1fe-793c-4f06-af17-d50d40598c082.MirrorCS"),sQuery(id+"F2.wireOp",EDGE,"729de1fe-793c-4f06-af17-d50d40598c083.MirrorCS"),sQuery(id+"F2.wireOp",EDGE,"729de1fe-793c-4f06-af17-d50d40598c084.MirrorCS"),sQuery(id+"F2.wireOp",EDGE,"729de1fe-793c-4f06-af17-d50d40598c085.MirrorCS"),sQuery(id+"F2.wireOp",EDGE,"729de1fe-793c-4f06-af17-d50d40598c086.MirrorCS"),sQuery(id+"F2.wireOp",EDGE,"729de1fe-793c-4f06-af17-d50d40598c087.MirrorCS"),sQuery(id+"F2.wireOp",EDGE,"729de1fe-793c-4f06-af17-d50d40598c088.MirrorCS"),sQuery(id+"F2.wireOp",EDGE,"729de1fe-793c-4f06-af17-d50d40598c089.MirrorCS"),sQuery(id+"F2.wireOp",EDGE,"E770.MirrorCS"),sQuery(id+"F2.wireOp",EDGE,"E78.MirrorCS"),sQuery(id+"F2.wireOp",EDGE,"E772.MirrorCS"),sQuery(id+"F2.wireOp",EDGE,"E79.MirrorCS"),sQuery(id+"F2.wireOp",EDGE,"E774.MirrorCS"),sQuery(id+"F2.wireOp",EDGE,"E775.MirrorCS"),sQuery(id+"F2.wireOp",EDGE,"E776.MirrorCS"),sQuery(id+"F2.wireOp",EDGE,"E777.MirrorCS"),sQuery(id+"F2.wireOp",EDGE,"E778.MirrorCS"),sQuery(id+"F2.wireOp",EDGE,"E779.MirrorCS"),sQuery(id+"F2.wireOp",EDGE,"729de1fe-793c-4f06-af17-d50d40598c0820.MirrorCS"),sQuery(id+"F2.wireOp",EDGE,"E80.MirrorCS"),sQuery(id+"F2.wireOp",EDGE,"E82.MirrorCS"),sQuery(id+"F2.wireOp",EDGE,"E83.MirrorCS"),sQuery(id+"F2.wireOp",EDGE,"E84.MirrorCS"),sQuery(id+"F2.wireOp",EDGE,"E85.MirrorCS"),sQuery(id+"F2.wireOp",EDGE,"E86.MirrorCS"),sQuery(id+"F2.wireOp",EDGE,"E92.MirrorCS"),sQuery(id+"F2.wireOp",EDGE,"729de1fe-793c-4f06-af17-d50d40598c0837.MirrorCS"),sQuery(id+"F2.wireOp",EDGE,"729de1fe-793c-4f06-af17-d50d40598c0838.MirrorCS"),sQuery(id+"F2.wireOp",EDGE,"729de1fe-793c-4f06-af17-d50d40598c0841.MirrorCS"),sQuery(id+"F2.wireOp",EDGE,"E95.MirrorCS"),sQuery(id+"F2.wireOp",EDGE,"729de1fe-793c-4f06-af17-d50d40598c0851.MirrorCS"),sQuery(id+"F2.wireOp",EDGE,"E89.MirrorCS"),sQuery(id+"F2.wireOp",EDGE,"E100.MirrorCS"),sQuery(id+"F2.wireOp",EDGE,"E101.MirrorCS"),sQuery(id+"F2.wireOp",EDGE,"E102.MirrorCS"),sQuery(id+"F2.wireOp",EDGE,"E104"),sQuery(id+"F2.wireOp",EDGE,"E105.MirrorCS"),sQuery(id+"F2.wireOp",EDGE,"E106.trimOffspring"),sQuery(id+"F2.wireOp",EDGE,"E108.MirrorCS"),sQuery(id+"F2.wireOp",EDGE,"E109.MirrorCS"),sQuery(id+"F2.wireOp",EDGE,"E110.trimOffspring"),sQuery(id+"F2.wireOp",EDGE,"31b2c9c2-f7eb-4751-8350-943a16306e17.trimOffspring"),sQuery(id+"F2.wireOp",EDGE,"E111.trimOffspring")])],"isStart":false}),"instanceName":"1"});
            var Q4;
            Q4=makeQuery(id+"F5.opPattern","COPY",FACE,{"derivedFrom":makeQuery(id+"F3.opExtrude","SWEPT_FACE",FACE,{"disambiguationData":[OSD([sQuery(id+"F2.wireOp",EDGE,"E59.bottom")])]}),"instanceName":"1"});
            var Q5;
            Q5=makeQuery(id+"F5.opPattern","COPY",FACE,{"derivedFrom":makeQuery(id+"F3.opExtrude","SWEPT_FACE",FACE,{"disambiguationData":[OSD([sQuery(id+"F2.wireOp",EDGE,"E60.top")])]}),"instanceName":"1"});
            var Q6;
            Q6=makeQuery(id+"F5.opPattern","COPY",FACE,{"derivedFrom":makeQuery(id+"F3.opExtrude","SWEPT_FACE",FACE,{"disambiguationData":[OSD([sQuery(id+"F2.wireOp",EDGE,"E62.bottom")])]}),"instanceName":"1"});
            var Q7;
            Q7=makeQuery(id+"F5.opPattern","COPY",FACE,{"derivedFrom":makeQuery(id+"F3.opExtrude","SWEPT_FACE",FACE,{"disambiguationData":[OSD([sQuery(id+"F2.wireOp",EDGE,"E65")])]}),"instanceName":"1"});
            var Q8;
            Q8=makeQuery(id+"F5.opPattern","COPY",FACE,{"derivedFrom":makeQuery(id+"F3.opExtrude","SWEPT_FACE",FACE,{"disambiguationData":[OSD([sQuery(id+"F2.wireOp",EDGE,"E64")])]}),"instanceName":"1"});
            var Q9;
            Q9=makeQuery(id+"F5.opPattern","COPY",FACE,{"derivedFrom":makeQuery(id+"F3.opExtrude","SWEPT_FACE",FACE,{"disambiguationData":[OSD([sQuery(id+"F2.wireOp",EDGE,"E66.trimOffspring")])]}),"instanceName":"1"});
            var Q10;
            Q10=makeQuery(id+"F5.opPattern","COPY",FACE,{"derivedFrom":makeQuery(id+"F3.opExtrude","SWEPT_FACE",FACE,{"disambiguationData":[OSD([sQuery(id+"F2.wireOp",EDGE,"E62.top")])]}),"instanceName":"1"});
            var Q11;
            Q11=makeQuery(id+"F5.opPattern","COPY",FACE,{"derivedFrom":makeQuery(id+"F3.opExtrude","SWEPT_FACE",FACE,{"disambiguationData":[OSD([sQuery(id+"F2.wireOp",EDGE,"E74")])]}),"instanceName":"1"});
            booleanBodies(context, id + "F6", {"operationType" : BooleanOperationType.SUBTRACTION, "tools" : qUnion([Q0]), "targets" : qUnion([Q1]), "offset" : true, "entitiesToOffset" : qUnion([Q2, Q3, Q4, Q5, Q6, Q7, Q8, Q9, Q10, Q11]), "offsetDistance" : 0.6 * mm, "keepTools" : true});
        }
        {
            var Q0;
            Q0=makeQuery(id+"F1.opExtrude","SWEPT_BODY",BODY,{"disambiguationData":[OSD([sQuery(id+"F0.wireOp",EDGE,"E0.bottom"),sQuery(id+"F0.wireOp",EDGE,"E0.top"),sQuery(id+"F0.wireOp",EDGE,"E0.left"),sQuery(id+"F0.wireOp",EDGE,"E0.right"),sQuery(id+"F0.wireOp",EDGE,"E3.trimOffspring"),sQuery(id+"F0.wireOp",EDGE,"E6.bottom"),sQuery(id+"F0.wireOp",EDGE,"E6.top"),sQuery(id+"F0.wireOp",EDGE,"E6.left"),sQuery(id+"F0.wireOp",EDGE,"E6.right"),sQuery(id+"F0.wireOp",EDGE,"E7.bottom"),sQuery(id+"F0.wireOp",EDGE,"E7.top"),sQuery(id+"F0.wireOp",EDGE,"E7.left"),sQuery(id+"F0.wireOp",EDGE,"E7.right"),sQuery(id+"F0.wireOp",EDGE,"1BBTkZs5-luX3-xtZO-tfno-nD7ZldyCOrRv"),sQuery(id+"F0.wireOp",EDGE,"E13.MirrorCS"),sQuery(id+"F0.wireOp",EDGE,"E14.MirrorCS"),sQuery(id+"F0.wireOp",EDGE,"E10.MirrorCS"),sQuery(id+"F0.wireOp",EDGE,"E15.MirrorCS"),sQuery(id+"F0.wireOp",EDGE,"edba22f7-fcec-4b76-9e19-08ec19d2e6a00.MirrorC"),sQuery(id+"F0.wireOp",EDGE,"E16.MirrorCS"),sQuery(id+"F0.wireOp",EDGE,"E17.MirrorCS"),sQuery(id+"F0.wireOp",EDGE,"E20.MirrorCS"),sQuery(id+"F0.wireOp",EDGE,"E21.MirrorCS"),sQuery(id+"F0.wireOp",EDGE,"E26.MirrorCS"),sQuery(id+"F0.wireOp",EDGE,"E27.MirrorCS"),sQuery(id+"F0.wireOp",EDGE,"E28.MirrorCS"),sQuery(id+"F0.wireOp",EDGE,"E29.MirrorCS"),sQuery(id+"F0.wireOp",EDGE,"e9cac41d-f357-42ad-afaa-485d0ff043840.MirrorC"),sQuery(id+"F0.wireOp",EDGE,"E30.MirrorCS"),sQuery(id+"F0.wireOp",EDGE,"E31.MirrorCS"),sQuery(id+"F0.wireOp",EDGE,"E32.MirrorCS"),sQuery(id+"F0.wireOp",EDGE,"E33.MirrorCS"),sQuery(id+"F0.wireOp",EDGE,"E34.MirrorCS"),sQuery(id+"F0.wireOp",EDGE,"E35.MirrorCS"),sQuery(id+"F0.wireOp",EDGE,"E36.MirrorCS"),sQuery(id+"F0.wireOp",EDGE,"E37.MirrorCS"),sQuery(id+"F0.wireOp",EDGE,"f40b6c40-3a45-4a40-b477-66a71d50dfa00.MirrorC"),sQuery(id+"F0.wireOp",EDGE,"E38.MirrorCS"),sQuery(id+"F0.wireOp",EDGE,"E39.MirrorCS"),sQuery(id+"F0.wireOp",EDGE,"E40.MirrorCS"),sQuery(id+"F0.wireOp",EDGE,"E41.MirrorCS"),sQuery(id+"F0.wireOp",EDGE,"E44.left"),sQuery(id+"F0.wireOp",EDGE,"E44.right"),sQuery(id+"F0.wireOp",EDGE,"eyhBYY9M-95YG-LpN2-QZ7T-SWmW0xq0itgo")])]});
            transform(context, id + "F7", {"entities" : qUnion([Q0]), "transformType" : TransformType.TRANSLATION_3D, "dx" : -205 * mm, "dy" : 0 * mm, "dz" : 0 * mm, "makeCopy" : true});
        }
    });
